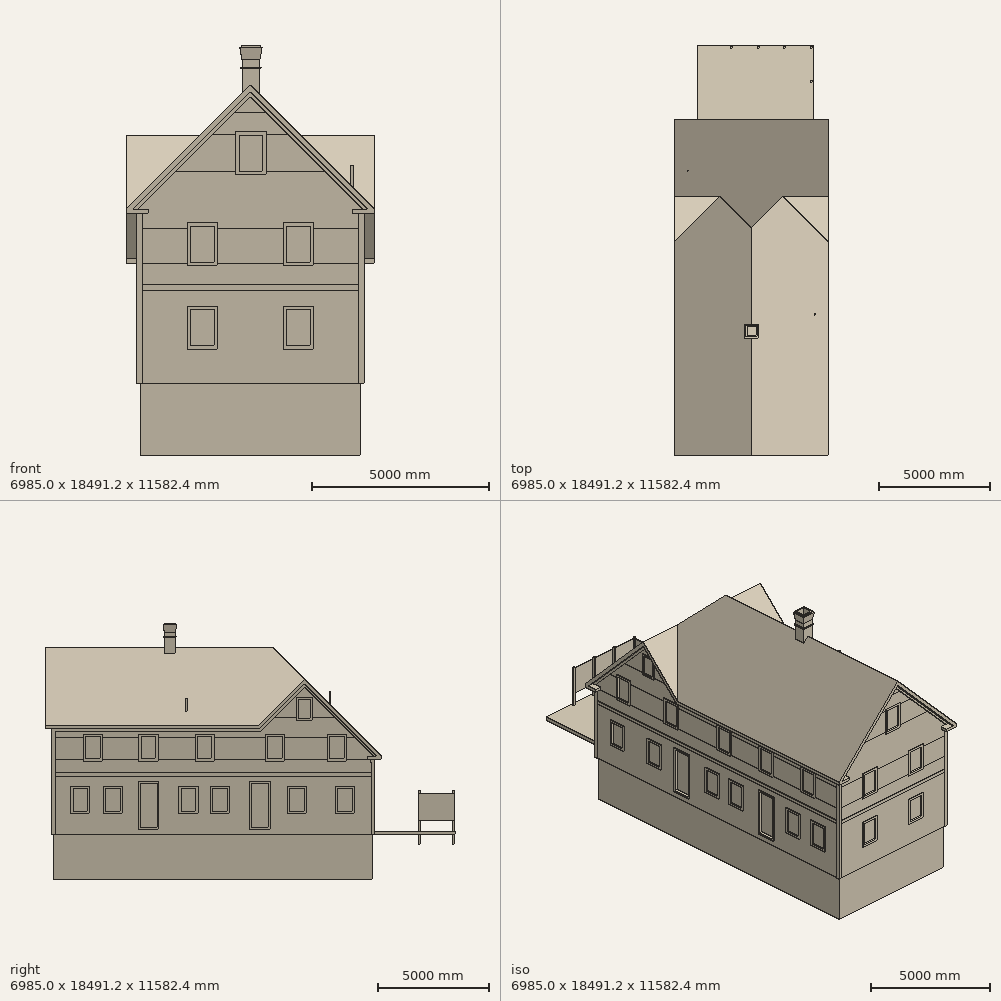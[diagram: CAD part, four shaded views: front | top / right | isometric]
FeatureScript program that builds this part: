
annotation { "Feature Type Name" : "Feature", "Feature Type Description" : "" }
export const myFeature = defineFeature(function(context is Context, id is Id, definition is map)
    precondition{}
    {
        {
            var Q0;
            Q0=qCreatedBy(makeId("Top.planeOp"),FACE);
            var sketch = newSketch(context, id + "F0", { "sketchPlane" : qUnion([Q0])});
            skLineSegment(sketch, "E0.bottom", {"start": v(0, 0) * mm, "end": v(-6985, 0) * mm});
            skLineSegment(sketch, "E0.top", {"start": v(0, 15138.4) * mm, "end": v(-6985, 15138.4) * mm});
            skLineSegment(sketch, "E0.left", {"start": v(0, 0) * mm, "end": v(0, 15138.4) * mm});
            skLineSegment(sketch, "E0.right", {"start": v(-6985, 0) * mm, "end": v(-6985, 15138.4) * mm});
            skSolve(sketch);
        }
        {
            var Q0;
            Q0 = qSketchRegion(id + "F0", true);
            extrude(context, id + "F1", {"entities" : qUnion([Q0]), "depth" : 4953 * mm});
        }
        {
            var Q0;
            Q0=makeQuery(id+"F1.opExtrude","SWEPT_FACE",FACE,{"disambiguationData":[OSD([sQuery(id+"F0.wireOp",EDGE,"E0.bottom")])]});
            var sketch = newSketch(context, id + "F2", { "sketchPlane" : qUnion([Q0])});
            skLineSegment(sketch, "E1", {"start": v(-6985, 4953) * mm, "end": v(0, 4953) * mm});
            skLineSegment(sketch, "E2", {"start": v(0, 4953) * mm, "end": v(-3492.5, 8445.5) * mm});
            skLineSegment(sketch, "E3", {"start": v(-3492.5, 8445.5) * mm, "end": v(-6985, 4953) * mm});
            skSolve(sketch);
        }
        {
            var Q0;
            Q0=makeQuery(id+"F2.imprint","IMPRINT",FACE,{"disambiguationData":[TD([[makeQuery(id+"F2.imprint","IMPRINT",EDGE,{"derivedFrom":sQuery(id+"F2.wireOp",EDGE,"E1")}),-1.0]])]});
            var Q1;
            Q1=makeQuery(id+"F1.opExtrude","SWEPT_FACE",FACE,{"disambiguationData":[OSD([sQuery(id+"F0.wireOp",EDGE,"E0.top")])]});
            extrude(context, id + "F3", {"entities" : qUnion([Q0]), "operationType" : NewBodyOperationType.ADD, "endBound" : BoundingType.UP_TO_SURFACE, "oppositeDirection" : true, "endBoundEntityFace" : qUnion([Q1]), "depth" : 25.4 * mm});
        }
        {
            var Q0;
            Q0=makeQuery(id+"F1.opExtrude","SWEPT_FACE",FACE,{"disambiguationData":[OSD([sQuery(id+"F0.wireOp",EDGE,"E0.left")])]});
            var sketch = newSketch(context, id + "F4", { "sketchPlane" : qUnion([Q0])});
            skLineSegment(sketch, "E4", {"start": v(15138.4, 3556) * mm, "end": v(10248.9, 8445.5) * mm});
            skLineSegment(sketch, "E5", {"start": v(10248.9, 8445.5) * mm, "end": v(15138.4, 8445.5) * mm});
            skLineSegment(sketch, "E6", {"start": v(15138.4, 8445.5) * mm, "end": v(15138.4, 3556) * mm});
            skSolve(sketch);
        }
        {
            var Q0;
            {var subQ0=sQuery(id+"F4.wireOp",EDGE,"E5");Q0=makeQuery(id+"F4.imprint","IMPRINT",FACE,{"disambiguationData":[TD([[makeQuery(id+"F4.imprint","IMPRINT",EDGE,{"derivedFrom":subQ0}),-1.0]])]});}
            var Q1;
            {var subQ0=sQuery(id+"F4.wireOp",EDGE,"E6");var subQ1=sQuery(id+"F4.wireOp",EDGE,"E4");var subQ2=sQuery(id+"F0.wireOp",EDGE,"E0.left");var subQ3=makeQuery(id+"F4.imprint","INTERSECT",VERTEX,{"derivedFrom":[makeQuery(id+"F1.opExtrude","SWEPT_EDGE",EDGE,{"disambiguationData":[OSD([sQuery(id+"F0.wireOp",EDGE,"E0.top"),subQ2])]}),subQ1,subQ0]});Q1=makeQuery(id+"F4.imprint","IMPRINT",FACE,{"disambiguationData":[TD([[makeQuery(id+"F4.imprint","IMPRINT",EDGE,{"disambiguationData":[TD([[subQ3,-1.0]])],"derivedFrom":subQ1}),-1.0]])]});}
            extrude(context, id + "F5", {"entities" : qUnion([Q0, Q1]), "operationType" : NewBodyOperationType.REMOVE, "endBound" : BoundingType.THROUGH_ALL, "oppositeDirection" : true, "depth" : 25.4 * mm});
        }
        {
            var Q0;
            Q0=makeQuery(id+"F1.opExtrude","SWEPT_FACE",FACE,{"disambiguationData":[OSD([sQuery(id+"F0.wireOp",EDGE,"E0.left")])]});
            var Q1;
            Q1=makeQuery(id+"F5.boolean.opBoolean","INTERSECT",VERTEX,{"derivedFrom":[makeQuery(id+"F3.opExtrude","SWEPT_FACE",FACE,{"disambiguationData":[OSD([sQuery(id+"F2.wireOp",EDGE,"E2")])]}),makeQuery(id+"F3.opExtrude","SWEPT_FACE",FACE,{"disambiguationData":[OSD([sQuery(id+"F2.wireOp",EDGE,"E3")])]}),makeQuery(id+"F5.opExtrude","SWEPT_FACE",FACE,{"disambiguationData":[OSD([sQuery(id+"F4.wireOp",EDGE,"E4")])]})]});
            cPlane(context, id + "F6", {"entities" : qUnion([Q0, Q1]), "cplaneType" : CPlaneType.PLANE_POINT, "offset" : 25.4 * mm, "width" : 152.4 * mm, "height" : 152.4 * mm});
        }
        {
            var Q0;
            Q0=qCreatedBy(id+"F6.planeOp",FACE);
            var sketch = newSketch(context, id + "F7", { "sketchPlane" : qUnion([Q0])});
            skLineSegment(sketch, "E7", {"start": v(11685.74, 7008.66) * mm, "end": v(9630.08, 4953) * mm});
            skLineSegment(sketch, "E8", {"start": v(11685.74, 7008.66) * mm, "end": v(15138.4, 3556) * mm});
            skLineSegment(sketch, "E9", {"start": v(15138.4, 3556) * mm, "end": v(9630.08, 4953) * mm});
            skSolve(sketch);
        }
        {
            var Q0;
            Q0 = qSketchRegion(id + "F7", true);
            var Q1;
            Q1=makeQuery(id+"F1.opExtrude","SWEPT_FACE",FACE,{"disambiguationData":[OSD([sQuery(id+"F0.wireOp",EDGE,"E0.left")])]});
            var Q2;
            Q2=makeQuery(id+"F1.opExtrude","SWEPT_FACE",FACE,{"disambiguationData":[OSD([sQuery(id+"F0.wireOp",EDGE,"E0.right")])]});
            extrude(context, id + "F8", {"entities" : qUnion([Q0]), "operationType" : NewBodyOperationType.ADD, "endBound" : BoundingType.UP_TO_SURFACE, "endBoundEntityFace" : qUnion([Q1]), "depth" : 25.4 * mm, "hasSecondDirection" : true, "secondDirectionBound" : SecondDirectionBoundingType.UP_TO_SURFACE, "secondDirectionOppositeDirection" : true, "secondDirectionBoundEntityFace" : qUnion([Q2]), "secondDirectionDepth" : 25.4 * mm});
        }
        {
            var Q0;
            Q0=makeQuery(id+"F8.boolean.opBoolean","MERGE",FACE,{"derivedFrom":[makeQuery(id+"F1.opExtrude","SWEPT_FACE",FACE,{"disambiguationData":[OSD([sQuery(id+"F0.wireOp",EDGE,"E0.left")])]}),makeQuery(id+"F8.opExtrude","CAP_FACE",FACE,{"disambiguationData":[OSD([sQuery(id+"F7.wireOp",EDGE,"E7"),sQuery(id+"F7.wireOp",EDGE,"E8"),sQuery(id+"F7.wireOp",EDGE,"E9")])],"isStart":false})]});
            var sketch = newSketch(context, id + "F9", { "sketchPlane" : qUnion([Q0])});
            skLineSegment(sketch, "E10", {"start": v(11685.74, 6793.13) * mm, "end": v(9630.08, 4737.47) * mm});
            skLineSegment(sketch, "E11", {"start": v(11685.74, 6793.13) * mm, "end": v(14948.27, 3530.6) * mm});
            skLineSegment(sketch, "E12", {"start": v(14948.27, 3530.6) * mm, "end": v(14528.8, 3530.6) * mm});
            skLineSegment(sketch, "E13", {"start": v(14528.8, 3530.6) * mm, "end": v(14528.8, 3403.6) * mm});
            skLineSegment(sketch, "E14", {"start": v(14528.8, 3403.6) * mm, "end": v(15303.14, 3403.6) * mm});
            skLineSegment(sketch, "E15", {"start": v(9630.08, 4737.47) * mm, "end": v(9630.08, 0) * mm});
            skLineSegment(sketch, "E16", {"start": v(9630.08, 0) * mm, "end": v(15138.4, 0) * mm});
            skLineSegment(sketch, "E17", {"start": v(15303.14, 3403.6) * mm, "end": v(15138.4, 0) * mm});
            skSolve(sketch);
        }
        {
            var Q0;
            Q0 = qSketchRegion(id + "F9", true);
            extrude(context, id + "F10", {"entities" : qUnion([Q0]), "operationType" : NewBodyOperationType.REMOVE, "oppositeDirection" : true, "depth" : 304.8 * mm});
        }
        {
            var Q0;
            Q0=makeQuery(id+"F8.boolean.opBoolean","MERGE",FACE,{"derivedFrom":[makeQuery(id+"F1.opExtrude","SWEPT_FACE",FACE,{"disambiguationData":[OSD([sQuery(id+"F0.wireOp",EDGE,"E0.right")])]}),makeQuery(id+"F8.opExtrude","CAP_FACE",FACE,{"disambiguationData":[OSD([sQuery(id+"F7.wireOp",EDGE,"E7"),sQuery(id+"F7.wireOp",EDGE,"E8"),sQuery(id+"F7.wireOp",EDGE,"E9")])],"isStart":true})]});
            var sketch = newSketch(context, id + "F11", { "sketchPlane" : qUnion([Q0])});
            skLineSegment(sketch, "E18.0.0", {"start": v(-15138.4, 0) * mm, "end": v(-15138.4, 3403.6) * mm});
            skLineSegment(sketch, "E18.0.1", {"start": v(-15138.4, 3403.6) * mm, "end": v(-14528.8, 3403.6) * mm});
            skLineSegment(sketch, "E18.0.2", {"start": v(-14528.8, 3403.6) * mm, "end": v(-14528.8, 3530.6) * mm});
            skLineSegment(sketch, "E18.0.3", {"start": v(-14528.8, 3530.6) * mm, "end": v(-14948.27, 3530.6) * mm});
            skLineSegment(sketch, "E18.0.4", {"start": v(-14948.27, 3530.6) * mm, "end": v(-11685.74, 6793.13) * mm});
            skLineSegment(sketch, "E18.0.5", {"start": v(-11685.74, 6793.13) * mm, "end": v(-9630.08, 4737.47) * mm});
            skLineSegment(sketch, "E18.0.6", {"start": v(-9630.08, 4737.47) * mm, "end": v(-9630.08, 0) * mm});
            skLineSegment(sketch, "E18.0.7", {"start": v(-9630.08, 0) * mm, "end": v(-15138.4, 0) * mm});
            skSolve(sketch);
        }
        {
            var Q0;
            Q0 = qSketchRegion(id + "F11", true);
            extrude(context, id + "F12", {"entities" : qUnion([Q0]), "operationType" : NewBodyOperationType.REMOVE, "oppositeDirection" : true, "depth" : 304.8 * mm});
        }
        {
            var Q0;
            Q0=makeQuery(id+"F10.boolean.opBoolean","COPY",FACE,{"derivedFrom":makeQuery(id+"F10.opExtrude","CAP_FACE",FACE,{"disambiguationData":[OSD([sQuery(id+"F9.wireOp",EDGE,"E10"),sQuery(id+"F9.wireOp",EDGE,"E11"),sQuery(id+"F9.wireOp",EDGE,"E12"),sQuery(id+"F9.wireOp",EDGE,"E13"),sQuery(id+"F9.wireOp",EDGE,"E14"),sQuery(id+"F9.wireOp",EDGE,"E15"),sQuery(id+"F9.wireOp",EDGE,"E16"),sQuery(id+"F9.wireOp",EDGE,"E17")])],"isStart":false})});
            var sketch = newSketch(context, id + "F13", { "sketchPlane" : qUnion([Q0])});
            skLineSegment(sketch, "E19.bottom", {"start": v(15138.4, 0) * mm, "end": v(14833.6, 0) * mm});
            skLineSegment(sketch, "E19.top", {"start": v(15138.4, 3403.6) * mm, "end": v(14833.6, 3403.6) * mm});
            skLineSegment(sketch, "E19.left", {"start": v(15138.4, 0) * mm, "end": v(15138.4, 3403.6) * mm});
            skLineSegment(sketch, "E19.right", {"start": v(14833.6, 0) * mm, "end": v(14833.6, 3403.6) * mm});
            skSolve(sketch);
        }
        {
            var Q0;
            Q0 = qSketchRegion(id + "F13", true);
            extrude(context, id + "F14", {"entities" : qUnion([Q0]), "operationType" : NewBodyOperationType.REMOVE, "endBound" : BoundingType.THROUGH_ALL, "oppositeDirection" : true, "depth" : 25.4 * mm});
        }
        {
            var Q0;
            Q0=makeQuery(id+"F3.boolean.opBoolean","MERGE",FACE,{"derivedFrom":[makeQuery(id+"F1.opExtrude","SWEPT_FACE",FACE,{"disambiguationData":[OSD([sQuery(id+"F0.wireOp",EDGE,"E0.bottom")])]}),makeQuery(id+"F3.opExtrude","CAP_FACE",FACE,{"disambiguationData":[OSD([sQuery(id+"F2.wireOp",EDGE,"E1"),sQuery(id+"F2.wireOp",EDGE,"E2"),sQuery(id+"F2.wireOp",EDGE,"E3")])],"isStart":true})]});
            var sketch = newSketch(context, id + "F15", { "sketchPlane" : qUnion([Q0])});
            skLineSegment(sketch, "E20", {"start": v(-3492.5, 8229.97) * mm, "end": v(-190.13, 4927.6) * mm});
            skLineSegment(sketch, "E21", {"start": v(-190.13, 4927.6) * mm, "end": v(-609.6, 4927.6) * mm});
            skLineSegment(sketch, "E22", {"start": v(-609.6, 4927.6) * mm, "end": v(-609.6, 4800.6) * mm});
            skLineSegment(sketch, "E23", {"start": v(-609.6, 4800.6) * mm, "end": v(323.7, 4800.6) * mm});
            skLineSegment(sketch, "E24", {"start": v(323.7, 4800.6) * mm, "end": v(323.7, 0) * mm});
            skLineSegment(sketch, "E25", {"start": v(323.7, 0) * mm, "end": v(-3492.5, 0) * mm});
            skLineSegment(sketch, "E26.MirrorCS", {"start": v(-7308.7, 0) * mm, "end": v(-3492.5, 0) * mm});
            skLineSegment(sketch, "E27.MirrorCS", {"start": v(-7308.7, 4800.6) * mm, "end": v(-7308.7, 0) * mm});
            skLineSegment(sketch, "E28.MirrorCS", {"start": v(-6375.4, 4800.6) * mm, "end": v(-7308.7, 4800.6) * mm});
            skLineSegment(sketch, "E29.MirrorCS", {"start": v(-6375.4, 4927.6) * mm, "end": v(-6375.4, 4800.6) * mm});
            skLineSegment(sketch, "E30.MirrorCS", {"start": v(-3492.5, 8229.97) * mm, "end": v(-6794.87, 4927.6) * mm});
            skLineSegment(sketch, "E31.MirrorCS", {"start": v(-6794.87, 4927.6) * mm, "end": v(-6375.4, 4927.6) * mm});
            skSolve(sketch);
        }
        {
            var Q0;
            Q0 = qSketchRegion(id + "F15", true);
            extrude(context, id + "F16", {"entities" : qUnion([Q0]), "operationType" : NewBodyOperationType.REMOVE, "oppositeDirection" : true, "depth" : 304.8 * mm});
        }
        {
            var Q0;
            Q0=makeQuery(id+"F16.boolean.opBoolean","COPY",FACE,{"derivedFrom":makeQuery(id+"F16.opExtrude","CAP_FACE",FACE,{"disambiguationData":[OSD([sQuery(id+"F15.wireOp",EDGE,"E20"),sQuery(id+"F15.wireOp",EDGE,"E21"),sQuery(id+"F15.wireOp",EDGE,"E22"),sQuery(id+"F15.wireOp",EDGE,"E23"),sQuery(id+"F15.wireOp",EDGE,"E24"),sQuery(id+"F15.wireOp",EDGE,"E25"),sQuery(id+"F15.wireOp",EDGE,"E26.MirrorCS"),sQuery(id+"F15.wireOp",EDGE,"E27.MirrorCS"),sQuery(id+"F15.wireOp",EDGE,"E28.MirrorCS"),sQuery(id+"F15.wireOp",EDGE,"E29.MirrorCS"),sQuery(id+"F15.wireOp",EDGE,"E30.MirrorCS"),sQuery(id+"F15.wireOp",EDGE,"E31.MirrorCS")])],"isStart":false})});
            var sketch = newSketch(context, id + "F17", { "sketchPlane" : qUnion([Q0])});
            skLineSegment(sketch, "E32.bottom", {"start": v(0, 0) * mm, "end": v(-304.8, 0) * mm});
            skLineSegment(sketch, "E32.top", {"start": v(0, 4800.6) * mm, "end": v(-304.8, 4800.6) * mm});
            skLineSegment(sketch, "E32.left", {"start": v(0, 0) * mm, "end": v(0, 4800.6) * mm});
            skLineSegment(sketch, "E32.right", {"start": v(-304.8, 0) * mm, "end": v(-304.8, 4800.6) * mm});
            skLineSegment(sketch, "E33.MirrorCS", {"start": v(-6985, 4800.6) * mm, "end": v(-6680.2, 4800.6) * mm});
            skLineSegment(sketch, "E34.MirrorCS", {"start": v(-6985, 0) * mm, "end": v(-6680.2, 0) * mm});
            skLineSegment(sketch, "E35.MirrorCS", {"start": v(-6680.2, 0) * mm, "end": v(-6680.2, 4800.6) * mm});
            skLineSegment(sketch, "E36.MirrorCS", {"start": v(-6985, 0) * mm, "end": v(-6985, 4800.6) * mm});
            skSolve(sketch);
        }
        {
            var Q0;
            Q0 = qSketchRegion(id + "F17", true);
            var Q1;
            Q1=makeQuery(id+"F10.boolean.opBoolean","COPY",FACE,{"derivedFrom":makeQuery(id+"F10.opExtrude","SWEPT_FACE",FACE,{"disambiguationData":[OSD([sQuery(id+"F9.wireOp",EDGE,"E15")])]})});
            extrude(context, id + "F18", {"entities" : qUnion([Q0]), "operationType" : NewBodyOperationType.REMOVE, "oppositeDirection" : true, "endBoundEntityFace" : qUnion([Q1]), "depth" : 10617.2 * mm});
        }
        {
            var Q0;
            Q0=makeQuery(id+"F14.boolean.opBoolean","MERGE",FACE,{"derivedFrom":[makeQuery(id+"F10.boolean.opBoolean","COPY",FACE,{"derivedFrom":makeQuery(id+"F10.opExtrude","SWEPT_FACE",FACE,{"disambiguationData":[OSD([sQuery(id+"F9.wireOp",EDGE,"E14")])]})}),makeQuery(id+"F12.boolean.opBoolean","COPY",FACE,{"derivedFrom":makeQuery(id+"F12.opExtrude","SWEPT_FACE",FACE,{"disambiguationData":[OSD([sQuery(id+"F11.wireOp",EDGE,"E18.0.1")])]})}),makeQuery(id+"F14.opExtrude","SWEPT_FACE",FACE,{"disambiguationData":[OSD([sQuery(id+"F13.wireOp",EDGE,"E19.top")])]})]});
            cPlane(context, id + "F19", {"entities" : qUnion([Q0]), "cplaneType" : CPlaneType.OFFSET, "offset" : 609.6 * mm, "width" : 152.4 * mm, "height" : 152.4 * mm});
        }
        {
            var Q0;
            Q0=qCreatedBy(id+"F19.planeOp",FACE);
            var sketch = newSketch(context, id + "F20", { "sketchPlane" : qUnion([Q0])});
            skLineSegment(sketch, "E37.0", {"start": v(-285.75, -285.75) * mm, "end": v(-6699.25, -285.75) * mm});
            skLineSegment(sketch, "E37.1", {"start": v(-285.75, -14852.65) * mm, "end": v(-285.75, -285.75) * mm});
            skLineSegment(sketch, "E37.2", {"start": v(-6699.25, -14852.65) * mm, "end": v(-285.75, -14852.65) * mm});
            skLineSegment(sketch, "E37.3", {"start": v(-6699.25, -285.75) * mm, "end": v(-6699.25, -14852.65) * mm});
            skSolve(sketch);
        }
        {
            var Q0;
            Q0 = qSketchRegion(id + "F20", true);
            extrude(context, id + "F21", {"entities" : qUnion([Q0]), "operationType" : NewBodyOperationType.ADD, "depth" : 152.4 * mm});
        }
        {
            var Q0;
            {var subQ1=sQuery(id+"F9.wireOp",EDGE,"E14");var subQ2=sQuery(id+"F9.wireOp",EDGE,"E10");var subQ3=sQuery(id+"F9.wireOp",EDGE,"E11");var subQ4=sQuery(id+"F9.wireOp",EDGE,"E13");var subQ5=sQuery(id+"F9.wireOp",EDGE,"E12");Q0=makeQuery(id+"F21.boolean.opBoolean","SPLIT",FACE,{"disambiguationData":[TD([makeQuery(id+"F10.boolean.opBoolean","COPY",FACE,{"derivedFrom":makeQuery(id+"F10.opExtrude","SWEPT_FACE",FACE,{"disambiguationData":[OSD([subQ2])]})})])],"derivedFrom":makeQuery(id+"F18.boolean.opBoolean","MERGE",FACE,{"derivedFrom":[makeQuery(id+"F10.boolean.opBoolean","COPY",FACE,{"derivedFrom":makeQuery(id+"F10.opExtrude","CAP_FACE",FACE,{"disambiguationData":[OSD([subQ2,subQ3,subQ5,subQ4,subQ1,sQuery(id+"F9.wireOp",EDGE,"E15"),sQuery(id+"F9.wireOp",EDGE,"E16"),sQuery(id+"F9.wireOp",EDGE,"E17")])],"isStart":false})}),makeQuery(id+"F18.opExtrude","SWEPT_FACE",FACE,{"disambiguationData":[OSD([sQuery(id+"F17.wireOp",EDGE,"E32.right")])]})]})});}
            var sketch = newSketch(context, id + "F22", { "sketchPlane" : qUnion([Q0])});
            skLineSegment(sketch, "E38", {"start": v(304.8, 4800.6) * mm, "end": v(304.8, 4648.2) * mm});
            skLineSegment(sketch, "E39", {"start": v(304.8, 4648.2) * mm, "end": v(9684.5, 4648.2) * mm});
            skLineSegment(sketch, "E40", {"start": v(9684.5, 4648.2) * mm, "end": v(11685.74, 6649.45) * mm});
            skLineSegment(sketch, "E41", {"start": v(11685.74, 6649.45) * mm, "end": v(14804.59, 3530.6) * mm});
            skSolve(sketch);
        }
        {
            var Q0;
            Q0=makeQuery(id+"F22.imprint","IMPRINT",FACE,{"disambiguationData":[TD([[makeQuery(id+"F22.imprint","IMPRINT",EDGE,{"derivedFrom":sQuery(id+"F22.wireOp",EDGE,"E38")}),-1.0]])]});
            extrude(context, id + "F23", {"entities" : qUnion([Q0]), "operationType" : NewBodyOperationType.ADD, "depth" : 25.4 * mm});
        }
        {
            var Q0;
            {var subQ1=sQuery(id+"F11.wireOp",EDGE,"E18.0.5");var subQ2=sQuery(id+"F11.wireOp",EDGE,"E18.0.2");var subQ3=sQuery(id+"F11.wireOp",EDGE,"E18.0.1");var subQ4=sQuery(id+"F11.wireOp",EDGE,"E18.0.4");var subQ5=sQuery(id+"F11.wireOp",EDGE,"E18.0.3");Q0=makeQuery(id+"F21.boolean.opBoolean","SPLIT",FACE,{"disambiguationData":[TD([makeQuery(id+"F10.boolean.opBoolean","COPY",FACE,{"derivedFrom":makeQuery(id+"F10.opExtrude","SWEPT_FACE",FACE,{"disambiguationData":[OSD([sQuery(id+"F9.wireOp",EDGE,"E14")])]})})])],"derivedFrom":makeQuery(id+"F18.boolean.opBoolean","MERGE",FACE,{"derivedFrom":[makeQuery(id+"F12.boolean.opBoolean","COPY",FACE,{"derivedFrom":makeQuery(id+"F12.opExtrude","CAP_FACE",FACE,{"disambiguationData":[OSD([sQuery(id+"F11.wireOp",EDGE,"E18.0.0"),subQ3,subQ2,subQ5,subQ4,subQ1,sQuery(id+"F11.wireOp",EDGE,"E18.0.6"),sQuery(id+"F11.wireOp",EDGE,"E18.0.7")])],"isStart":false})}),makeQuery(id+"F18.opExtrude","SWEPT_FACE",FACE,{"disambiguationData":[OSD([sQuery(id+"F17.wireOp",EDGE,"E35.MirrorCS")])]})]})});}
            var sketch = newSketch(context, id + "F24", { "sketchPlane" : qUnion([Q0])});
            skLineSegment(sketch, "E42.0.0", {"start": v(-304.8, 4800.6) * mm, "end": v(-304.8, 4648.2) * mm});
            skLineSegment(sketch, "E42.0.1", {"start": v(-304.8, 4648.2) * mm, "end": v(-9684.5, 4648.2) * mm});
            skLineSegment(sketch, "E42.0.2", {"start": v(-9684.5, 4648.2) * mm, "end": v(-11685.74, 6649.45) * mm});
            skLineSegment(sketch, "E42.0.3", {"start": v(-11685.74, 6649.45) * mm, "end": v(-14804.59, 3530.6) * mm});
            skLineSegment(sketch, "E42.0.4", {"start": v(-14804.59, 3530.6) * mm, "end": v(-14948.27, 3530.6) * mm});
            skLineSegment(sketch, "E42.0.5", {"start": v(-14948.27, 3530.6) * mm, "end": v(-11685.74, 6793.13) * mm});
            skLineSegment(sketch, "E42.0.6", {"start": v(-11685.74, 6793.13) * mm, "end": v(-9693.2, 4800.6) * mm});
            skLineSegment(sketch, "E42.0.7", {"start": v(-9693.2, 4800.6) * mm, "end": v(-304.8, 4800.6) * mm});
            skSolve(sketch);
        }
        {
            var Q0;
            Q0 = qSketchRegion(id + "F24", true);
            extrude(context, id + "F25", {"entities" : qUnion([Q0]), "operationType" : NewBodyOperationType.ADD, "depth" : 25.4 * mm});
        }
        {
            var Q0;
            {var subQ0=sQuery(id+"F15.wireOp",EDGE,"E31.MirrorCS");var subQ1=sQuery(id+"F15.wireOp",EDGE,"E30.MirrorCS");var subQ2=sQuery(id+"F15.wireOp",EDGE,"E29.MirrorCS");var subQ3=sQuery(id+"F15.wireOp",EDGE,"E28.MirrorCS");var subQ4=sQuery(id+"F15.wireOp",EDGE,"E23");var subQ5=sQuery(id+"F15.wireOp",EDGE,"E22");var subQ6=sQuery(id+"F15.wireOp",EDGE,"E21");var subQ7=sQuery(id+"F15.wireOp",EDGE,"E20");Q0=makeQuery(id+"F25.boolean.opBoolean","MERGE",FACE,{"derivedFrom":[makeQuery(id+"F23.boolean.opBoolean","MERGE",FACE,{"derivedFrom":[makeQuery(id+"F21.boolean.opBoolean","SPLIT",FACE,{"disambiguationData":[TD([makeQuery(id+"F16.boolean.opBoolean","COPY",FACE,{"derivedFrom":makeQuery(id+"F16.opExtrude","SWEPT_FACE",FACE,{"disambiguationData":[OSD([subQ7])]})})])],"derivedFrom":makeQuery(id+"F16.boolean.opBoolean","COPY",FACE,{"derivedFrom":makeQuery(id+"F16.opExtrude","CAP_FACE",FACE,{"disambiguationData":[OSD([subQ7,subQ6,subQ5,subQ4,sQuery(id+"F15.wireOp",EDGE,"E24"),sQuery(id+"F15.wireOp",EDGE,"E25"),sQuery(id+"F15.wireOp",EDGE,"E26.MirrorCS"),sQuery(id+"F15.wireOp",EDGE,"E27.MirrorCS"),subQ3,subQ2,subQ1,subQ0])],"isStart":false})})}),makeQuery(id+"F23.opExtrude","SWEPT_FACE",FACE,{"disambiguationData":[OSD([sQuery(id+"F22.wireOp",EDGE,"E38")])]})]}),makeQuery(id+"F25.opExtrude","SWEPT_FACE",FACE,{"disambiguationData":[OSD([sQuery(id+"F24.wireOp",EDGE,"E42.0.0")])]})]});}
            var sketch = newSketch(context, id + "F26", { "sketchPlane" : qUnion([Q0])});
            skLineSegment(sketch, "E43", {"start": v(-6651.19, 4927.6) * mm, "end": v(-3492.5, 8086.29) * mm});
            skLineSegment(sketch, "E44", {"start": v(-3492.5, 8086.29) * mm, "end": v(-333.81, 4927.6) * mm});
            skSolve(sketch);
        }
        {
            var Q0;
            {var subQ5=sQuery(id+"F26.wireOp",EDGE,"E43");Q0=makeQuery(id+"F26.imprint","IMPRINT",FACE,{"disambiguationData":[TD([[makeQuery(id+"F26.imprint","IMPRINT",EDGE,{"derivedFrom":subQ5}),1.0]])]});}
            extrude(context, id + "F27", {"entities" : qUnion([Q0]), "operationType" : NewBodyOperationType.ADD, "depth" : 25.4 * mm});
        }
        {
            var Q0;
            {var subQ1=sQuery(id+"F9.wireOp",EDGE,"E14");var subQ2=sQuery(id+"F9.wireOp",EDGE,"E10");var subQ3=sQuery(id+"F9.wireOp",EDGE,"E11");var subQ4=sQuery(id+"F9.wireOp",EDGE,"E13");var subQ5=sQuery(id+"F9.wireOp",EDGE,"E12");Q0=makeQuery(id+"F21.boolean.opBoolean","SPLIT",FACE,{"disambiguationData":[TD([makeQuery(id+"F10.boolean.opBoolean","COPY",FACE,{"derivedFrom":makeQuery(id+"F10.opExtrude","SWEPT_FACE",FACE,{"disambiguationData":[OSD([subQ2])]})})])],"derivedFrom":makeQuery(id+"F18.boolean.opBoolean","MERGE",FACE,{"derivedFrom":[makeQuery(id+"F10.boolean.opBoolean","COPY",FACE,{"derivedFrom":makeQuery(id+"F10.opExtrude","CAP_FACE",FACE,{"disambiguationData":[OSD([subQ2,subQ3,subQ5,subQ4,subQ1,sQuery(id+"F9.wireOp",EDGE,"E15"),sQuery(id+"F9.wireOp",EDGE,"E16"),sQuery(id+"F9.wireOp",EDGE,"E17")])],"isStart":false})}),makeQuery(id+"F18.opExtrude","SWEPT_FACE",FACE,{"disambiguationData":[OSD([sQuery(id+"F17.wireOp",EDGE,"E32.right")])]})]})});}
            var sketch = newSketch(context, id + "F28", { "sketchPlane" : qUnion([Q0])});
            skLineSegment(sketch, "E45.bottom", {"start": v(14655.8, 3251.2) * mm, "end": v(14859, 3251.2) * mm});
            skLineSegment(sketch, "E45.top", {"start": v(14655.8, 3403.6) * mm, "end": v(14859, 3403.6) * mm});
            skLineSegment(sketch, "E45.left", {"start": v(14655.8, 3251.2) * mm, "end": v(14655.8, 3403.6) * mm});
            skLineSegment(sketch, "E45.right", {"start": v(14859, 3251.2) * mm, "end": v(14859, 3403.6) * mm});
            skSolve(sketch);
        }
        {
            var Q0;
            Q0 = qSketchRegion(id + "F28", true);
            extrude(context, id + "F29", {"entities" : qUnion([Q0]), "operationType" : NewBodyOperationType.ADD, "depth" : 25.4 * mm, "hasSecondDirection" : true, "secondDirectionOppositeDirection" : true, "secondDirectionDepth" : 6400.8 * mm});
        }
        {
            var Q0;
            Q0=makeQuery(id+"F1.opExtrude","CAP_FACE",FACE,{"disambiguationData":[OSD([sQuery(id+"F0.wireOp",EDGE,"E0.bottom"),sQuery(id+"F0.wireOp",EDGE,"E0.top"),sQuery(id+"F0.wireOp",EDGE,"E0.left"),sQuery(id+"F0.wireOp",EDGE,"E0.right")])],"isStart":true});
            var sketch = newSketch(context, id + "F30", { "sketchPlane" : qUnion([Q0])});
            skLineSegment(sketch, "E46.bottom", {"start": v(-431.8, -279.4) * mm, "end": v(-279.4, -279.4) * mm});
            skLineSegment(sketch, "E46.top", {"start": v(-431.8, -431.8) * mm, "end": v(-279.4, -431.8) * mm});
            skLineSegment(sketch, "E46.left", {"start": v(-431.8, -279.4) * mm, "end": v(-431.8, -431.8) * mm});
            skLineSegment(sketch, "E46.right", {"start": v(-279.4, -279.4) * mm, "end": v(-279.4, -431.8) * mm});
            skLineSegment(sketch, "E47", {"start": v(-3492.5, -304.8) * mm, "end": v(-3492.5, -1029.25) * mm});
            skPoint(sketch, "E47.endSnap0", {"position": v(-3492.5, -304.8) * mm});
            skLineSegment(sketch, "E48.MirrorCS", {"start": v(-6553.2, -279.4) * mm, "end": v(-6705.6, -279.4) * mm});
            skLineSegment(sketch, "E49.MirrorCS", {"start": v(-6553.2, -431.8) * mm, "end": v(-6705.6, -431.8) * mm});
            skLineSegment(sketch, "E50.MirrorCS", {"start": v(-6553.2, -279.4) * mm, "end": v(-6553.2, -431.8) * mm});
            skLineSegment(sketch, "E51.MirrorCS", {"start": v(-6705.6, -279.4) * mm, "end": v(-6705.6, -431.8) * mm});
            skSolve(sketch);
        }
        {
            var Q0;
            Q0 = qSketchRegion(id + "F30", true);
            var Q1;
            Q1=makeQuery(id+"F18.boolean.opBoolean","MERGE",FACE,{"derivedFrom":[makeQuery(id+"F16.boolean.opBoolean","COPY",FACE,{"derivedFrom":makeQuery(id+"F16.opExtrude","SWEPT_FACE",FACE,{"disambiguationData":[OSD([sQuery(id+"F15.wireOp",EDGE,"E28.MirrorCS")])]})}),makeQuery(id+"F18.opExtrude","SWEPT_FACE",FACE,{"disambiguationData":[OSD([sQuery(id+"F17.wireOp",EDGE,"E33.MirrorCS")])]})]});
            extrude(context, id + "F31", {"entities" : qUnion([Q0]), "operationType" : NewBodyOperationType.ADD, "endBound" : BoundingType.UP_TO_SURFACE, "oppositeDirection" : true, "endBoundEntityFace" : qUnion([Q1]), "depth" : 25.4 * mm});
        }
        {
            var Q0;
            Q0=makeQuery(id+"F31.boolean.opBoolean","MERGE",FACE,{"derivedFrom":[makeQuery(id+"F1.opExtrude","CAP_FACE",FACE,{"disambiguationData":[OSD([sQuery(id+"F0.wireOp",EDGE,"E0.bottom"),sQuery(id+"F0.wireOp",EDGE,"E0.top"),sQuery(id+"F0.wireOp",EDGE,"E0.left"),sQuery(id+"F0.wireOp",EDGE,"E0.right")])],"isStart":true}),makeQuery(id+"F31.opExtrude","CAP_FACE",FACE,{"disambiguationData":[OSD([sQuery(id+"F30.wireOp",EDGE,"E46.bottom"),sQuery(id+"F30.wireOp",EDGE,"E46.top"),sQuery(id+"F30.wireOp",EDGE,"E46.left"),sQuery(id+"F30.wireOp",EDGE,"E46.right")])],"isStart":true}),makeQuery(id+"F31.opExtrude","CAP_FACE",FACE,{"disambiguationData":[OSD([sQuery(id+"F30.wireOp",EDGE,"E48.MirrorCS"),sQuery(id+"F30.wireOp",EDGE,"E49.MirrorCS"),sQuery(id+"F30.wireOp",EDGE,"E50.MirrorCS"),sQuery(id+"F30.wireOp",EDGE,"E51.MirrorCS")])],"isStart":true})]});
            var sketch = newSketch(context, id + "F32", { "sketchPlane" : qUnion([Q0])});
            skLineSegment(sketch, "E52.bottom", {"start": v(-6553.2, -14706.6) * mm, "end": v(-6705.6, -14706.6) * mm});
            skLineSegment(sketch, "E52.top", {"start": v(-6553.2, -14859) * mm, "end": v(-6705.6, -14859) * mm});
            skLineSegment(sketch, "E52.left", {"start": v(-6553.2, -14706.6) * mm, "end": v(-6553.2, -14859) * mm});
            skLineSegment(sketch, "E52.right", {"start": v(-6705.6, -14706.6) * mm, "end": v(-6705.6, -14859) * mm});
            skLineSegment(sketch, "E53", {"start": v(-3492.5, -14833.6) * mm, "end": v(-3492.5, -14090.53) * mm});
            skLineSegment(sketch, "E54.MirrorCS", {"start": v(-431.8, -14706.6) * mm, "end": v(-431.8, -14859) * mm});
            skLineSegment(sketch, "E55.MirrorCS", {"start": v(-279.4, -14706.6) * mm, "end": v(-279.4, -14859) * mm});
            skLineSegment(sketch, "E56.MirrorCS", {"start": v(-431.8, -14706.6) * mm, "end": v(-279.4, -14706.6) * mm});
            skLineSegment(sketch, "E57.MirrorCS", {"start": v(-431.8, -14859) * mm, "end": v(-279.4, -14859) * mm});
            skSolve(sketch);
        }
        {
            var Q0;
            Q0 = qSketchRegion(id + "F32", true);
            var Q1;
            Q1=makeQuery(id+"F14.boolean.opBoolean","MERGE",FACE,{"derivedFrom":[makeQuery(id+"F10.boolean.opBoolean","COPY",FACE,{"derivedFrom":makeQuery(id+"F10.opExtrude","SWEPT_FACE",FACE,{"disambiguationData":[OSD([sQuery(id+"F9.wireOp",EDGE,"E14")])]})}),makeQuery(id+"F12.boolean.opBoolean","COPY",FACE,{"derivedFrom":makeQuery(id+"F12.opExtrude","SWEPT_FACE",FACE,{"disambiguationData":[OSD([sQuery(id+"F11.wireOp",EDGE,"E18.0.1")])]})}),makeQuery(id+"F14.opExtrude","SWEPT_FACE",FACE,{"disambiguationData":[OSD([sQuery(id+"F13.wireOp",EDGE,"E19.top")])]})]});
            extrude(context, id + "F33", {"entities" : qUnion([Q0]), "operationType" : NewBodyOperationType.ADD, "endBound" : BoundingType.UP_TO_SURFACE, "oppositeDirection" : true, "endBoundEntityFace" : qUnion([Q1]), "depth" : 25.4 * mm});
        }
        {
            var Q0;
            {var subQ1=sQuery(id+"F9.wireOp",EDGE,"E14");var subQ2=sQuery(id+"F9.wireOp",EDGE,"E10");var subQ3=sQuery(id+"F9.wireOp",EDGE,"E11");var subQ4=sQuery(id+"F9.wireOp",EDGE,"E13");var subQ5=sQuery(id+"F9.wireOp",EDGE,"E12");Q0=makeQuery(id+"F21.boolean.opBoolean","SPLIT",FACE,{"disambiguationData":[TD([makeQuery(id+"F10.boolean.opBoolean","COPY",FACE,{"derivedFrom":makeQuery(id+"F10.opExtrude","SWEPT_FACE",FACE,{"disambiguationData":[OSD([subQ2])]})})])],"derivedFrom":makeQuery(id+"F18.boolean.opBoolean","MERGE",FACE,{"derivedFrom":[makeQuery(id+"F10.boolean.opBoolean","COPY",FACE,{"derivedFrom":makeQuery(id+"F10.opExtrude","CAP_FACE",FACE,{"disambiguationData":[OSD([subQ2,subQ3,subQ5,subQ4,subQ1,sQuery(id+"F9.wireOp",EDGE,"E15"),sQuery(id+"F9.wireOp",EDGE,"E16"),sQuery(id+"F9.wireOp",EDGE,"E17")])],"isStart":false})}),makeQuery(id+"F18.opExtrude","SWEPT_FACE",FACE,{"disambiguationData":[OSD([sQuery(id+"F17.wireOp",EDGE,"E32.right")])]})]})});}
            var sketch = newSketch(context, id + "F34", { "sketchPlane" : qUnion([Q0])});
            skLineSegment(sketch, "E58", {"start": v(14528.8, 3403.6) * mm, "end": v(431.8, 3403.6) * mm});
            skLineSegment(sketch, "E59", {"start": v(431.8, 4394.2) * mm, "end": v(13940.99, 4394.2) * mm});
            skLineSegment(sketch, "E60", {"start": v(10314.14, 5277.85) * mm, "end": v(13057.34, 5277.85) * mm});
            skSolve(sketch);
        }
        {
            var Q0;
            {var subQ0=sQuery(id+"F34.wireOp",EDGE,"E60");Q0=makeQuery(id+"F34.imprint","IMPRINT",FACE,{"disambiguationData":[TD([[makeQuery(id+"F34.imprint","IMPRINT",EDGE,{"derivedFrom":subQ0}),1.0]])]});}
            var Q1;
            {var subQ4=sQuery(id+"F34.wireOp",EDGE,"E58");Q1=makeQuery(id+"F34.imprint","IMPRINT",FACE,{"disambiguationData":[TD([[makeQuery(id+"F34.imprint","IMPRINT",EDGE,{"derivedFrom":subQ4}),-1.0]])]});}
            extrude(context, id + "F35", {"entities" : qUnion([Q0, Q1]), "operationType" : NewBodyOperationType.ADD, "depth" : 6.35 * mm});
        }
        {
            var Q0;
            {var subQ1=sQuery(id+"F11.wireOp",EDGE,"E18.0.5");var subQ2=sQuery(id+"F11.wireOp",EDGE,"E18.0.2");var subQ3=sQuery(id+"F11.wireOp",EDGE,"E18.0.1");var subQ4=sQuery(id+"F11.wireOp",EDGE,"E18.0.4");var subQ5=sQuery(id+"F11.wireOp",EDGE,"E18.0.3");Q0=makeQuery(id+"F21.boolean.opBoolean","SPLIT",FACE,{"disambiguationData":[TD([makeQuery(id+"F10.boolean.opBoolean","COPY",FACE,{"derivedFrom":makeQuery(id+"F10.opExtrude","SWEPT_FACE",FACE,{"disambiguationData":[OSD([sQuery(id+"F9.wireOp",EDGE,"E14")])]})})])],"derivedFrom":makeQuery(id+"F18.boolean.opBoolean","MERGE",FACE,{"derivedFrom":[makeQuery(id+"F12.boolean.opBoolean","COPY",FACE,{"derivedFrom":makeQuery(id+"F12.opExtrude","CAP_FACE",FACE,{"disambiguationData":[OSD([sQuery(id+"F11.wireOp",EDGE,"E18.0.0"),subQ3,subQ2,subQ5,subQ4,subQ1,sQuery(id+"F11.wireOp",EDGE,"E18.0.6"),sQuery(id+"F11.wireOp",EDGE,"E18.0.7")])],"isStart":false})}),makeQuery(id+"F18.opExtrude","SWEPT_FACE",FACE,{"disambiguationData":[OSD([sQuery(id+"F17.wireOp",EDGE,"E35.MirrorCS")])]})]})});}
            var sketch = newSketch(context, id + "F36", { "sketchPlane" : qUnion([Q0])});
            skLineSegment(sketch, "E61.0.0", {"start": v(-431.8, 3403.6) * mm, "end": v(-14528.8, 3403.6) * mm});
            skLineSegment(sketch, "E61.0.1", {"start": v(-14528.8, 3403.6) * mm, "end": v(-14528.8, 3530.6) * mm});
            skLineSegment(sketch, "E61.0.2", {"start": v(-14528.8, 3530.6) * mm, "end": v(-14804.59, 3530.6) * mm});
            skLineSegment(sketch, "E61.0.3", {"start": v(-14804.59, 3530.6) * mm, "end": v(-13940.99, 4394.2) * mm});
            skLineSegment(sketch, "E61.0.4", {"start": v(-13940.99, 4394.2) * mm, "end": v(-431.8, 4394.2) * mm});
            skLineSegment(sketch, "E61.0.5", {"start": v(-431.8, 4394.2) * mm, "end": v(-431.8, 3403.6) * mm});
            skLineSegment(sketch, "E61.1.0", {"start": v(-11685.74, 6649.45) * mm, "end": v(-10314.14, 5277.85) * mm});
            skLineSegment(sketch, "E61.1.1", {"start": v(-10314.14, 5277.85) * mm, "end": v(-13057.34, 5277.85) * mm});
            skLineSegment(sketch, "E61.1.2", {"start": v(-13057.34, 5277.85) * mm, "end": v(-11685.74, 6649.45) * mm});
            skSolve(sketch);
        }
        {
            var Q0;
            Q0=makeQuery(id+"F36.imprint","IMPRINT",FACE,{"disambiguationData":[TD([[makeQuery(id+"F36.imprint","IMPRINT",EDGE,{"derivedFrom":sQuery(id+"F36.wireOp",EDGE,"E61.0.0")}),-1.0]])]});
            var Q1;
            Q1=makeQuery(id+"F36.imprint","IMPRINT",FACE,{"disambiguationData":[TD([[makeQuery(id+"F36.imprint","IMPRINT",EDGE,{"derivedFrom":sQuery(id+"F36.wireOp",EDGE,"E61.1.0")}),1.0]])]});
            extrude(context, id + "F37", {"entities" : qUnion([Q0, Q1]), "operationType" : NewBodyOperationType.ADD, "depth" : 6.35 * mm});
        }
        {
            var Q0;
            {var subQ0=sQuery(id+"F15.wireOp",EDGE,"E31.MirrorCS");var subQ1=sQuery(id+"F15.wireOp",EDGE,"E30.MirrorCS");var subQ2=sQuery(id+"F15.wireOp",EDGE,"E29.MirrorCS");var subQ3=sQuery(id+"F15.wireOp",EDGE,"E28.MirrorCS");var subQ4=sQuery(id+"F15.wireOp",EDGE,"E23");var subQ5=sQuery(id+"F15.wireOp",EDGE,"E22");var subQ6=sQuery(id+"F15.wireOp",EDGE,"E21");var subQ7=sQuery(id+"F15.wireOp",EDGE,"E20");Q0=makeQuery(id+"F25.boolean.opBoolean","MERGE",FACE,{"derivedFrom":[makeQuery(id+"F23.boolean.opBoolean","MERGE",FACE,{"derivedFrom":[makeQuery(id+"F21.boolean.opBoolean","SPLIT",FACE,{"disambiguationData":[TD([makeQuery(id+"F16.boolean.opBoolean","COPY",FACE,{"derivedFrom":makeQuery(id+"F16.opExtrude","SWEPT_FACE",FACE,{"disambiguationData":[OSD([subQ7])]})})])],"derivedFrom":makeQuery(id+"F16.boolean.opBoolean","COPY",FACE,{"derivedFrom":makeQuery(id+"F16.opExtrude","CAP_FACE",FACE,{"disambiguationData":[OSD([subQ7,subQ6,subQ5,subQ4,sQuery(id+"F15.wireOp",EDGE,"E24"),sQuery(id+"F15.wireOp",EDGE,"E25"),sQuery(id+"F15.wireOp",EDGE,"E26.MirrorCS"),sQuery(id+"F15.wireOp",EDGE,"E27.MirrorCS"),subQ3,subQ2,subQ1,subQ0])],"isStart":false})})}),makeQuery(id+"F23.opExtrude","SWEPT_FACE",FACE,{"disambiguationData":[OSD([sQuery(id+"F22.wireOp",EDGE,"E38")])]})]}),makeQuery(id+"F25.opExtrude","SWEPT_FACE",FACE,{"disambiguationData":[OSD([sQuery(id+"F24.wireOp",EDGE,"E42.0.0")])]})]});}
            var sketch = newSketch(context, id + "F38", { "sketchPlane" : qUnion([Q0])});
            skLineSegment(sketch, "E62", {"start": v(-6553.2, 3403.6) * mm, "end": v(-431.8, 3403.6) * mm});
            skLineSegment(sketch, "E63", {"start": v(-6553.2, 4394.2) * mm, "end": v(-431.8, 4394.2) * mm});
            skLineSegment(sketch, "E64", {"start": v(-5575.3, 6003.49) * mm, "end": v(-1409.7, 6003.49) * mm});
            skSolve(sketch);
        }
        {
            var Q0;
            {var subQ0=sQuery(id+"F38.wireOp",EDGE,"E64");Q0=makeQuery(id+"F38.imprint","IMPRINT",FACE,{"disambiguationData":[TD([[makeQuery(id+"F38.imprint","IMPRINT",EDGE,{"derivedFrom":subQ0}),1.0]])]});}
            var Q1;
            {var subQ0=sQuery(id+"F38.wireOp",EDGE,"E62");Q1=makeQuery(id+"F38.imprint","IMPRINT",FACE,{"disambiguationData":[TD([[makeQuery(id+"F38.imprint","IMPRINT",EDGE,{"derivedFrom":subQ0}),1.0]])]});}
            extrude(context, id + "F39", {"entities" : qUnion([Q0, Q1]), "operationType" : NewBodyOperationType.ADD, "depth" : 6.35 * mm});
        }
        {
            var Q0;
            Q0=makeQuery(id+"F33.boolean.opBoolean","MERGE",FACE,{"derivedFrom":[makeQuery(id+"F31.boolean.opBoolean","MERGE",FACE,{"derivedFrom":[makeQuery(id+"F1.opExtrude","CAP_FACE",FACE,{"disambiguationData":[OSD([sQuery(id+"F0.wireOp",EDGE,"E0.bottom"),sQuery(id+"F0.wireOp",EDGE,"E0.top"),sQuery(id+"F0.wireOp",EDGE,"E0.left"),sQuery(id+"F0.wireOp",EDGE,"E0.right")])],"isStart":true}),makeQuery(id+"F31.opExtrude","CAP_FACE",FACE,{"disambiguationData":[OSD([sQuery(id+"F30.wireOp",EDGE,"E46.bottom"),sQuery(id+"F30.wireOp",EDGE,"E46.top"),sQuery(id+"F30.wireOp",EDGE,"E46.left"),sQuery(id+"F30.wireOp",EDGE,"E46.right")])],"isStart":true}),makeQuery(id+"F31.opExtrude","CAP_FACE",FACE,{"disambiguationData":[OSD([sQuery(id+"F30.wireOp",EDGE,"E48.MirrorCS"),sQuery(id+"F30.wireOp",EDGE,"E49.MirrorCS"),sQuery(id+"F30.wireOp",EDGE,"E50.MirrorCS"),sQuery(id+"F30.wireOp",EDGE,"E51.MirrorCS")])],"isStart":true})]}),makeQuery(id+"F33.opExtrude","CAP_FACE",FACE,{"disambiguationData":[OSD([sQuery(id+"F32.wireOp",EDGE,"E52.bottom"),sQuery(id+"F32.wireOp",EDGE,"E52.top"),sQuery(id+"F32.wireOp",EDGE,"E52.left"),sQuery(id+"F32.wireOp",EDGE,"E52.right")])],"isStart":true}),makeQuery(id+"F33.opExtrude","CAP_FACE",FACE,{"disambiguationData":[OSD([sQuery(id+"F32.wireOp",EDGE,"E54.MirrorCS"),sQuery(id+"F32.wireOp",EDGE,"E55.MirrorCS"),sQuery(id+"F32.wireOp",EDGE,"E56.MirrorCS"),sQuery(id+"F32.wireOp",EDGE,"E57.MirrorCS")])],"isStart":true})]});
            var sketch = newSketch(context, id + "F40", { "sketchPlane" : qUnion([Q0])});
            skLineSegment(sketch, "E65.bottom", {"start": v(-3732.4, -5867.4) * mm, "end": v(-3224.4, -5867.4) * mm});
            skLineSegment(sketch, "E65.top", {"start": v(-3732.4, -5359.4) * mm, "end": v(-3224.4, -5359.4) * mm});
            skLineSegment(sketch, "E65.left", {"start": v(-3732.4, -5867.4) * mm, "end": v(-3732.4, -5359.4) * mm});
            skLineSegment(sketch, "E65.right", {"start": v(-3224.4, -5867.4) * mm, "end": v(-3224.4, -5359.4) * mm});
            skSolve(sketch);
        }
        {
            var Q0;
            Q0 = qSketchRegion(id + "F40", true);
            extrude(context, id + "F41", {"entities" : qUnion([Q0]), "operationType" : NewBodyOperationType.ADD, "oppositeDirection" : true, "depth" : 8890 * mm});
        }
        {
            var Q0;
            Q0=makeQuery(id+"F41.opExtrude","CAP_FACE",FACE,{"disambiguationData":[OSD([sQuery(id+"F40.wireOp",EDGE,"E65.bottom"),sQuery(id+"F40.wireOp",EDGE,"E65.top"),sQuery(id+"F40.wireOp",EDGE,"E65.left"),sQuery(id+"F40.wireOp",EDGE,"E65.right")])],"isStart":false});
            var sketch = newSketch(context, id + "F42", { "sketchPlane" : qUnion([Q0])});
            skLineSegment(sketch, "E66.0", {"start": v(-3770.5, 5905.5) * mm, "end": v(-3770.5, 5321.3) * mm});
            skLineSegment(sketch, "E66.1", {"start": v(-3186.3, 5905.5) * mm, "end": v(-3770.5, 5905.5) * mm});
            skLineSegment(sketch, "E66.2", {"start": v(-3186.3, 5321.3) * mm, "end": v(-3186.3, 5905.5) * mm});
            skLineSegment(sketch, "E66.3", {"start": v(-3770.5, 5321.3) * mm, "end": v(-3186.3, 5321.3) * mm});
            skSolve(sketch);
        }
        {
            var Q0;
            Q0 = qSketchRegion(id + "F42", true);
            extrude(context, id + "F43", {"entities" : qUnion([Q0]), "operationType" : NewBodyOperationType.ADD, "depth" : 50.8 * mm});
        }
        {
            var Q0;
            Q0=makeQuery(id+"F43.opExtrude","CAP_FACE",FACE,{"disambiguationData":[OSD([sQuery(id+"F42.wireOp",EDGE,"E66.0"),sQuery(id+"F42.wireOp",EDGE,"E66.1"),sQuery(id+"F42.wireOp",EDGE,"E66.2"),sQuery(id+"F42.wireOp",EDGE,"E66.3")])],"isStart":false});
            var sketch = newSketch(context, id + "F44", { "sketchPlane" : qUnion([Q0])});
            skLineSegment(sketch, "E67.0", {"start": v(-3224.4, 5867.4) * mm, "end": v(-3732.4, 5867.4) * mm});
            skLineSegment(sketch, "E67.1", {"start": v(-3224.4, 5359.4) * mm, "end": v(-3224.4, 5867.4) * mm});
            skLineSegment(sketch, "E67.2", {"start": v(-3732.4, 5359.4) * mm, "end": v(-3224.4, 5359.4) * mm});
            skLineSegment(sketch, "E67.3", {"start": v(-3732.4, 5867.4) * mm, "end": v(-3732.4, 5359.4) * mm});
            skSolve(sketch);
        }
        {
            var Q0;
            Q0 = qSketchRegion(id + "F44", true);
            extrude(context, id + "F45", {"entities" : qUnion([Q0]), "operationType" : NewBodyOperationType.ADD, "depth" : 203.2 * mm});
        }
        {
            var Q0;
            Q0=makeQuery(id+"F45.opExtrude","CAP_FACE",FACE,{"disambiguationData":[OSD([sQuery(id+"F44.wireOp",EDGE,"E67.0"),sQuery(id+"F44.wireOp",EDGE,"E67.1"),sQuery(id+"F44.wireOp",EDGE,"E67.2"),sQuery(id+"F44.wireOp",EDGE,"E67.3")])],"isStart":false});
            var sketch = newSketch(context, id + "F46", { "sketchPlane" : qUnion([Q0])});
            skLineSegment(sketch, "E68.0.0", {"start": v(-3224.4, 5359.4) * mm, "end": v(-3224.4, 5867.4) * mm});
            skLineSegment(sketch, "E68.0.1", {"start": v(-3224.4, 5867.4) * mm, "end": v(-3732.4, 5867.4) * mm});
            skLineSegment(sketch, "E68.0.2", {"start": v(-3732.4, 5867.4) * mm, "end": v(-3732.4, 5359.4) * mm});
            skLineSegment(sketch, "E68.0.3", {"start": v(-3732.4, 5359.4) * mm, "end": v(-3224.4, 5359.4) * mm});
            skSolve(sketch);
        }
        {
            var Q0;
            Q0 = qSketchRegion(id + "F46", true);
            extrude(context, id + "F47", {"entities" : qUnion([Q0]), "operationType" : NewBodyOperationType.ADD, "depth" : 355.6 * mm, "hasDraft" : true, "draftAngle" : 10 * degree});
        }
        {
            var Q0;
            Q0=makeQuery(id+"F47.opExtrude","CAP_FACE",FACE,{"disambiguationData":[OSD([sQuery(id+"F46.wireOp",EDGE,"E68.0.0"),sQuery(id+"F46.wireOp",EDGE,"E68.0.1"),sQuery(id+"F46.wireOp",EDGE,"E68.0.2"),sQuery(id+"F46.wireOp",EDGE,"E68.0.3")])],"isStart":false});
            var sketch = newSketch(context, id + "F48", { "sketchPlane" : qUnion([Q0])});
            skLineSegment(sketch, "E69.0", {"start": v(-3744.3, 5347.5) * mm, "end": v(-3212.5, 5347.5) * mm});
            skLineSegment(sketch, "E69.1", {"start": v(-3744.3, 5879.3) * mm, "end": v(-3744.3, 5347.5) * mm});
            skLineSegment(sketch, "E69.2", {"start": v(-3212.5, 5879.3) * mm, "end": v(-3744.3, 5879.3) * mm});
            skLineSegment(sketch, "E69.3", {"start": v(-3212.5, 5347.5) * mm, "end": v(-3212.5, 5879.3) * mm});
            skSolve(sketch);
        }
        {
            var Q0;
            Q0 = qSketchRegion(id + "F48", true);
            extrude(context, id + "F49", {"entities" : qUnion([Q0]), "operationType" : NewBodyOperationType.ADD, "depth" : 50.8 * mm});
        }
        {
            var Q0;
            Q0=makeQuery(id+"F49.opExtrude","CAP_FACE",FACE,{"disambiguationData":[OSD([sQuery(id+"F48.wireOp",EDGE,"E69.0"),sQuery(id+"F48.wireOp",EDGE,"E69.1"),sQuery(id+"F48.wireOp",EDGE,"E69.2"),sQuery(id+"F48.wireOp",EDGE,"E69.3")])],"isStart":false});
            var sketch = newSketch(context, id + "F50", { "sketchPlane" : qUnion([Q0])});
            skLineSegment(sketch, "E70.0", {"start": v(-3693.5, 5828.5) * mm, "end": v(-3693.5, 5398.3) * mm});
            skLineSegment(sketch, "E70.1", {"start": v(-3263.3, 5828.5) * mm, "end": v(-3693.5, 5828.5) * mm});
            skLineSegment(sketch, "E70.2", {"start": v(-3263.3, 5398.3) * mm, "end": v(-3263.3, 5828.5) * mm});
            skLineSegment(sketch, "E70.3", {"start": v(-3693.5, 5398.3) * mm, "end": v(-3263.3, 5398.3) * mm});
            skSolve(sketch);
        }
        {
            var Q0;
            Q0 = qSketchRegion(id + "F50", true);
            extrude(context, id + "F51", {"entities" : qUnion([Q0]), "operationType" : NewBodyOperationType.REMOVE, "oppositeDirection" : true, "depth" : 508 * mm});
        }
        {
            var Q0;
            Q0=makeQuery(id+"F33.boolean.opBoolean","MERGE",FACE,{"derivedFrom":[makeQuery(id+"F31.boolean.opBoolean","MERGE",FACE,{"derivedFrom":[makeQuery(id+"F1.opExtrude","CAP_FACE",FACE,{"disambiguationData":[OSD([sQuery(id+"F0.wireOp",EDGE,"E0.bottom"),sQuery(id+"F0.wireOp",EDGE,"E0.top"),sQuery(id+"F0.wireOp",EDGE,"E0.left"),sQuery(id+"F0.wireOp",EDGE,"E0.right")])],"isStart":true}),makeQuery(id+"F31.opExtrude","CAP_FACE",FACE,{"disambiguationData":[OSD([sQuery(id+"F30.wireOp",EDGE,"E46.bottom"),sQuery(id+"F30.wireOp",EDGE,"E46.top"),sQuery(id+"F30.wireOp",EDGE,"E46.left"),sQuery(id+"F30.wireOp",EDGE,"E46.right")])],"isStart":true}),makeQuery(id+"F31.opExtrude","CAP_FACE",FACE,{"disambiguationData":[OSD([sQuery(id+"F30.wireOp",EDGE,"E48.MirrorCS"),sQuery(id+"F30.wireOp",EDGE,"E49.MirrorCS"),sQuery(id+"F30.wireOp",EDGE,"E50.MirrorCS"),sQuery(id+"F30.wireOp",EDGE,"E51.MirrorCS")])],"isStart":true})]}),makeQuery(id+"F33.opExtrude","CAP_FACE",FACE,{"disambiguationData":[OSD([sQuery(id+"F32.wireOp",EDGE,"E52.bottom"),sQuery(id+"F32.wireOp",EDGE,"E52.top"),sQuery(id+"F32.wireOp",EDGE,"E52.left"),sQuery(id+"F32.wireOp",EDGE,"E52.right")])],"isStart":true}),makeQuery(id+"F33.opExtrude","CAP_FACE",FACE,{"disambiguationData":[OSD([sQuery(id+"F32.wireOp",EDGE,"E54.MirrorCS"),sQuery(id+"F32.wireOp",EDGE,"E55.MirrorCS"),sQuery(id+"F32.wireOp",EDGE,"E56.MirrorCS"),sQuery(id+"F32.wireOp",EDGE,"E57.MirrorCS")])],"isStart":true})]});
            var sketch = newSketch(context, id + "F52", { "sketchPlane" : qUnion([Q0])});
            skLineSegment(sketch, "E71.0", {"start": v(-6604, -14757.4) * mm, "end": v(-381, -14757.4) * mm});
            skLineSegment(sketch, "E71.1", {"start": v(-6604, -381) * mm, "end": v(-6604, -14757.4) * mm});
            skLineSegment(sketch, "E71.2", {"start": v(-381, -381) * mm, "end": v(-6604, -381) * mm});
            skLineSegment(sketch, "E71.3", {"start": v(-381, -14757.4) * mm, "end": v(-381, -381) * mm});
            skSolve(sketch);
        }
        {
            var Q0;
            Q0 = qSketchRegion(id + "F52", true);
            extrude(context, id + "F53", {"entities" : qUnion([Q0]), "operationType" : NewBodyOperationType.ADD, "depth" : 2032 * mm});
        }
        {
            var Q0;
            Q0=makeQuery(id+"F21.boolean.opBoolean","SPLIT",FACE,{"disambiguationData":[TD([makeQuery(id+"F1.opExtrude","CAP_FACE",FACE,{"disambiguationData":[OSD([sQuery(id+"F0.wireOp",EDGE,"E0.bottom"),sQuery(id+"F0.wireOp",EDGE,"E0.top"),sQuery(id+"F0.wireOp",EDGE,"E0.left"),sQuery(id+"F0.wireOp",EDGE,"E0.right")])],"isStart":true})])],"derivedFrom":makeQuery(id+"F18.boolean.opBoolean","MERGE",FACE,{"derivedFrom":[makeQuery(id+"F10.boolean.opBoolean","COPY",FACE,{"derivedFrom":makeQuery(id+"F10.opExtrude","CAP_FACE",FACE,{"disambiguationData":[OSD([sQuery(id+"F9.wireOp",EDGE,"E10"),sQuery(id+"F9.wireOp",EDGE,"E11"),sQuery(id+"F9.wireOp",EDGE,"E12"),sQuery(id+"F9.wireOp",EDGE,"E13"),sQuery(id+"F9.wireOp",EDGE,"E14"),sQuery(id+"F9.wireOp",EDGE,"E15"),sQuery(id+"F9.wireOp",EDGE,"E16"),sQuery(id+"F9.wireOp",EDGE,"E17")])],"isStart":false})}),makeQuery(id+"F18.opExtrude","SWEPT_FACE",FACE,{"disambiguationData":[OSD([sQuery(id+"F17.wireOp",EDGE,"E32.right")])]})]})});
            var sketch = newSketch(context, id + "F54", { "sketchPlane" : qUnion([Q0])});
            skLineSegment(sketch, "E72.bottom", {"start": v(1143, 2184.4) * mm, "end": v(2006.6, 2184.4) * mm});
            skLineSegment(sketch, "E72.top", {"start": v(1143, 965.2) * mm, "end": v(2006.6, 965.2) * mm});
            skLineSegment(sketch, "E72.left", {"start": v(1143, 2184.4) * mm, "end": v(1143, 965.2) * mm});
            skLineSegment(sketch, "E72.right", {"start": v(2006.6, 2184.4) * mm, "end": v(2006.6, 965.2) * mm});
            skLineSegment(sketch, "E73.bottom", {"start": v(2616.2, 2184.4) * mm, "end": v(3479.8, 2184.4) * mm});
            skLineSegment(sketch, "E73.top", {"start": v(2616.2, 965.2) * mm, "end": v(3479.8, 965.2) * mm});
            skLineSegment(sketch, "E73.left", {"start": v(2616.2, 2184.4) * mm, "end": v(2616.2, 965.2) * mm});
            skLineSegment(sketch, "E73.right", {"start": v(3479.8, 2184.4) * mm, "end": v(3479.8, 965.2) * mm});
            skLineSegment(sketch, "E74.bottom", {"start": v(6019.8, 2184.4) * mm, "end": v(6883.4, 2184.4) * mm});
            skLineSegment(sketch, "E74.top", {"start": v(6019.8, 965.2) * mm, "end": v(6883.4, 965.2) * mm});
            skLineSegment(sketch, "E74.left", {"start": v(6019.8, 2184.4) * mm, "end": v(6019.8, 965.2) * mm});
            skLineSegment(sketch, "E74.right", {"start": v(6883.4, 2184.4) * mm, "end": v(6883.4, 965.2) * mm});
            skLineSegment(sketch, "E75.bottom", {"start": v(7442.2, 2184.4) * mm, "end": v(8305.8, 2184.4) * mm});
            skLineSegment(sketch, "E75.top", {"start": v(7442.2, 965.2) * mm, "end": v(8305.8, 965.2) * mm});
            skLineSegment(sketch, "E75.left", {"start": v(7442.2, 2184.4) * mm, "end": v(7442.2, 965.2) * mm});
            skLineSegment(sketch, "E75.right", {"start": v(8305.8, 2184.4) * mm, "end": v(8305.8, 965.2) * mm});
            skLineSegment(sketch, "E76.bottom", {"start": v(10896.6, 2184.4) * mm, "end": v(11760.2, 2184.4) * mm});
            skLineSegment(sketch, "E76.top", {"start": v(10896.6, 965.2) * mm, "end": v(11760.2, 965.2) * mm});
            skLineSegment(sketch, "E76.left", {"start": v(10896.6, 2184.4) * mm, "end": v(10896.6, 965.2) * mm});
            skLineSegment(sketch, "E76.right", {"start": v(11760.2, 2184.4) * mm, "end": v(11760.2, 965.2) * mm});
            skLineSegment(sketch, "E77.bottom", {"start": v(13081, 2184.4) * mm, "end": v(13944.6, 2184.4) * mm});
            skLineSegment(sketch, "E77.top", {"start": v(13081, 965.2) * mm, "end": v(13944.6, 965.2) * mm});
            skLineSegment(sketch, "E77.left", {"start": v(13081, 2184.4) * mm, "end": v(13081, 965.2) * mm});
            skLineSegment(sketch, "E77.right", {"start": v(13944.6, 2184.4) * mm, "end": v(13944.6, 965.2) * mm});
            skLineSegment(sketch, "E78.bottom", {"start": v(4191, 2387.6) * mm, "end": v(5105.4, 2387.6) * mm});
            skLineSegment(sketch, "E78.top", {"start": v(4191, 254) * mm, "end": v(5105.4, 254) * mm});
            skLineSegment(sketch, "E78.left", {"start": v(4191, 2387.6) * mm, "end": v(4191, 254) * mm});
            skLineSegment(sketch, "E78.right", {"start": v(5105.4, 2387.6) * mm, "end": v(5105.4, 254) * mm});
            skLineSegment(sketch, "E79.bottom", {"start": v(9220.2, 2387.6) * mm, "end": v(10134.6, 2387.6) * mm});
            skLineSegment(sketch, "E79.top", {"start": v(9220.2, 254) * mm, "end": v(10134.6, 254) * mm});
            skLineSegment(sketch, "E79.left", {"start": v(9220.2, 2387.6) * mm, "end": v(9220.2, 254) * mm});
            skLineSegment(sketch, "E79.right", {"start": v(10134.6, 2387.6) * mm, "end": v(10134.6, 254) * mm});
            skLineSegment(sketch, "E80.bottom", {"start": v(1701.8, 4546.6) * mm, "end": v(2565.4, 4546.6) * mm});
            skLineSegment(sketch, "E80.top", {"start": v(1701.8, 3327.4) * mm, "end": v(2565.4, 3327.4) * mm});
            skLineSegment(sketch, "E80.left", {"start": v(1701.8, 4546.6) * mm, "end": v(1701.8, 3327.4) * mm});
            skLineSegment(sketch, "E80.right", {"start": v(2565.4, 4546.6) * mm, "end": v(2565.4, 3327.4) * mm});
            skLineSegment(sketch, "E81.bottom", {"start": v(4216.4, 4546.6) * mm, "end": v(5080, 4546.6) * mm});
            skLineSegment(sketch, "E81.top", {"start": v(4216.4, 3327.4) * mm, "end": v(5080, 3327.4) * mm});
            skLineSegment(sketch, "E81.left", {"start": v(4216.4, 4546.6) * mm, "end": v(4216.4, 3327.4) * mm});
            skLineSegment(sketch, "E81.right", {"start": v(5080, 4546.6) * mm, "end": v(5080, 3327.4) * mm});
            skLineSegment(sketch, "E82.bottom", {"start": v(6744.89, 4546.6) * mm, "end": v(7608.49, 4546.6) * mm});
            skLineSegment(sketch, "E82.top", {"start": v(6744.89, 3327.4) * mm, "end": v(7608.49, 3327.4) * mm});
            skLineSegment(sketch, "E82.left", {"start": v(6744.89, 4546.6) * mm, "end": v(6744.89, 3327.4) * mm});
            skLineSegment(sketch, "E82.right", {"start": v(7608.49, 4546.6) * mm, "end": v(7608.49, 3327.4) * mm});
            skLineSegment(sketch, "E83.bottom", {"start": v(9906, 4546.6) * mm, "end": v(10769.6, 4546.6) * mm});
            skLineSegment(sketch, "E83.top", {"start": v(9906, 3327.4) * mm, "end": v(10769.6, 3327.4) * mm});
            skLineSegment(sketch, "E83.left", {"start": v(9906, 4546.6) * mm, "end": v(9906, 3327.4) * mm});
            skLineSegment(sketch, "E83.right", {"start": v(10769.6, 4546.6) * mm, "end": v(10769.6, 3327.4) * mm});
            skLineSegment(sketch, "E84.bottom", {"start": v(12725.4, 4546.6) * mm, "end": v(13589, 4546.6) * mm});
            skLineSegment(sketch, "E84.top", {"start": v(12725.4, 3327.4) * mm, "end": v(13589, 3327.4) * mm});
            skLineSegment(sketch, "E84.left", {"start": v(12725.4, 4546.6) * mm, "end": v(12725.4, 3327.4) * mm});
            skLineSegment(sketch, "E84.right", {"start": v(13589, 4546.6) * mm, "end": v(13589, 3327.4) * mm});
            skLineSegment(sketch, "E85.bottom", {"start": v(11328.4, 6192.25) * mm, "end": v(12039.6, 6192.25) * mm});
            skLineSegment(sketch, "E85.top", {"start": v(11328.4, 5176.25) * mm, "end": v(12039.6, 5176.25) * mm});
            skLineSegment(sketch, "E85.left", {"start": v(11328.4, 6192.25) * mm, "end": v(11328.4, 5176.25) * mm});
            skLineSegment(sketch, "E85.right", {"start": v(12039.6, 6192.25) * mm, "end": v(12039.6, 5176.25) * mm});
            skSolve(sketch);
        }
        {
            var Q0;
            Q0 = qSketchRegion(id + "F54", true);
            extrude(context, id + "F55", {"entities" : qUnion([Q0]), "operationType" : NewBodyOperationType.ADD, "depth" : 25.4 * mm, "hasSecondDirection" : true, "secondDirectionOppositeDirection" : true, "secondDirectionDepth" : 6400.8 * mm});
        }
        {
            var Q0;
            Q0=makeQuery(id+"F55.opExtrude","CAP_FACE",FACE,{"disambiguationData":[OSD([sQuery(id+"F54.wireOp",EDGE,"E72.bottom"),sQuery(id+"F54.wireOp",EDGE,"E72.top"),sQuery(id+"F54.wireOp",EDGE,"E72.left"),sQuery(id+"F54.wireOp",EDGE,"E72.right")])],"isStart":false});
            var sketch = newSketch(context, id + "F56", { "sketchPlane" : qUnion([Q0])});
            skLineSegment(sketch, "E86.0", {"start": v(1905, 2082.8) * mm, "end": v(1244.6, 2082.8) * mm});
            skLineSegment(sketch, "E86.1", {"start": v(1905, 1066.8) * mm, "end": v(1905, 2082.8) * mm});
            skLineSegment(sketch, "E86.2", {"start": v(1244.6, 1066.8) * mm, "end": v(1905, 1066.8) * mm});
            skLineSegment(sketch, "E86.3", {"start": v(1244.6, 2082.8) * mm, "end": v(1244.6, 1066.8) * mm});
            skLineSegment(sketch, "E87.0", {"start": v(3378.2, 2082.8) * mm, "end": v(2717.8, 2082.8) * mm});
            skLineSegment(sketch, "E87.1", {"start": v(3378.2, 1066.8) * mm, "end": v(3378.2, 2082.8) * mm});
            skLineSegment(sketch, "E87.2", {"start": v(2717.8, 1066.8) * mm, "end": v(3378.2, 1066.8) * mm});
            skLineSegment(sketch, "E87.3", {"start": v(2717.8, 2082.8) * mm, "end": v(2717.8, 1066.8) * mm});
            skLineSegment(sketch, "E88.0", {"start": v(6781.8, 2082.8) * mm, "end": v(6121.4, 2082.8) * mm});
            skLineSegment(sketch, "E88.1", {"start": v(6781.8, 1066.8) * mm, "end": v(6781.8, 2082.8) * mm});
            skLineSegment(sketch, "E88.2", {"start": v(6121.4, 1066.8) * mm, "end": v(6781.8, 1066.8) * mm});
            skLineSegment(sketch, "E88.3", {"start": v(6121.4, 2082.8) * mm, "end": v(6121.4, 1066.8) * mm});
            skLineSegment(sketch, "E89.0", {"start": v(8204.2, 2082.8) * mm, "end": v(7543.8, 2082.8) * mm});
            skLineSegment(sketch, "E89.1", {"start": v(8204.2, 1066.8) * mm, "end": v(8204.2, 2082.8) * mm});
            skLineSegment(sketch, "E89.2", {"start": v(7543.8, 1066.8) * mm, "end": v(8204.2, 1066.8) * mm});
            skLineSegment(sketch, "E89.3", {"start": v(7543.8, 2082.8) * mm, "end": v(7543.8, 1066.8) * mm});
            skLineSegment(sketch, "E90.0", {"start": v(11658.6, 2082.8) * mm, "end": v(10998.2, 2082.8) * mm});
            skLineSegment(sketch, "E90.1", {"start": v(11658.6, 1066.8) * mm, "end": v(11658.6, 2082.8) * mm});
            skLineSegment(sketch, "E90.2", {"start": v(10998.2, 1066.8) * mm, "end": v(11658.6, 1066.8) * mm});
            skLineSegment(sketch, "E90.3", {"start": v(10998.2, 2082.8) * mm, "end": v(10998.2, 1066.8) * mm});
            skLineSegment(sketch, "E91.0", {"start": v(13843, 2082.8) * mm, "end": v(13182.6, 2082.8) * mm});
            skLineSegment(sketch, "E91.1", {"start": v(13843, 1066.8) * mm, "end": v(13843, 2082.8) * mm});
            skLineSegment(sketch, "E91.2", {"start": v(13182.6, 1066.8) * mm, "end": v(13843, 1066.8) * mm});
            skLineSegment(sketch, "E91.3", {"start": v(13182.6, 2082.8) * mm, "end": v(13182.6, 1066.8) * mm});
            skLineSegment(sketch, "E92.0", {"start": v(2463.8, 4445) * mm, "end": v(1803.4, 4445) * mm});
            skLineSegment(sketch, "E92.1", {"start": v(2463.8, 3429) * mm, "end": v(2463.8, 4445) * mm});
            skLineSegment(sketch, "E92.2", {"start": v(1803.4, 3429) * mm, "end": v(2463.8, 3429) * mm});
            skLineSegment(sketch, "E92.3", {"start": v(1803.4, 4445) * mm, "end": v(1803.4, 3429) * mm});
            skLineSegment(sketch, "E93.0", {"start": v(4978.4, 4445) * mm, "end": v(4318, 4445) * mm});
            skLineSegment(sketch, "E93.1", {"start": v(4978.4, 3429) * mm, "end": v(4978.4, 4445) * mm});
            skLineSegment(sketch, "E93.2", {"start": v(4318, 3429) * mm, "end": v(4978.4, 3429) * mm});
            skLineSegment(sketch, "E93.3", {"start": v(4318, 4445) * mm, "end": v(4318, 3429) * mm});
            skLineSegment(sketch, "E94.0", {"start": v(7506.89, 4445) * mm, "end": v(6846.49, 4445) * mm});
            skLineSegment(sketch, "E94.1", {"start": v(7506.89, 3429) * mm, "end": v(7506.89, 4445) * mm});
            skLineSegment(sketch, "E94.2", {"start": v(6846.49, 3429) * mm, "end": v(7506.89, 3429) * mm});
            skLineSegment(sketch, "E94.3", {"start": v(6846.49, 4445) * mm, "end": v(6846.49, 3429) * mm});
            skLineSegment(sketch, "E95.0", {"start": v(10668, 4445) * mm, "end": v(10007.6, 4445) * mm});
            skLineSegment(sketch, "E95.1", {"start": v(10668, 3429) * mm, "end": v(10668, 4445) * mm});
            skLineSegment(sketch, "E95.2", {"start": v(10007.6, 3429) * mm, "end": v(10668, 3429) * mm});
            skLineSegment(sketch, "E95.3", {"start": v(10007.6, 4445) * mm, "end": v(10007.6, 3429) * mm});
            skLineSegment(sketch, "E96.0", {"start": v(13487.4, 4445) * mm, "end": v(12827, 4445) * mm});
            skLineSegment(sketch, "E96.1", {"start": v(13487.4, 3429) * mm, "end": v(13487.4, 4445) * mm});
            skLineSegment(sketch, "E96.2", {"start": v(12827, 3429) * mm, "end": v(13487.4, 3429) * mm});
            skLineSegment(sketch, "E96.3", {"start": v(12827, 4445) * mm, "end": v(12827, 3429) * mm});
            skLineSegment(sketch, "E97.0", {"start": v(11963.4, 6116.05) * mm, "end": v(11404.6, 6116.05) * mm});
            skLineSegment(sketch, "E97.1", {"start": v(11963.4, 5252.45) * mm, "end": v(11963.4, 6116.05) * mm});
            skLineSegment(sketch, "E97.2", {"start": v(11404.6, 5252.45) * mm, "end": v(11963.4, 5252.45) * mm});
            skLineSegment(sketch, "E97.3", {"start": v(11404.6, 6116.05) * mm, "end": v(11404.6, 5252.45) * mm});
            skLineSegment(sketch, "E98.0", {"start": v(5029.2, 2311.4) * mm, "end": v(4267.2, 2311.4) * mm});
            skLineSegment(sketch, "E98.1", {"start": v(5029.2, 330.2) * mm, "end": v(5029.2, 2311.4) * mm});
            skLineSegment(sketch, "E98.2", {"start": v(4267.2, 330.2) * mm, "end": v(5029.2, 330.2) * mm});
            skLineSegment(sketch, "E98.3", {"start": v(4267.2, 2311.4) * mm, "end": v(4267.2, 330.2) * mm});
            skLineSegment(sketch, "E99.0", {"start": v(10058.4, 2311.4) * mm, "end": v(9296.4, 2311.4) * mm});
            skLineSegment(sketch, "E99.1", {"start": v(10058.4, 330.2) * mm, "end": v(10058.4, 2311.4) * mm});
            skLineSegment(sketch, "E99.2", {"start": v(9296.4, 330.2) * mm, "end": v(10058.4, 330.2) * mm});
            skLineSegment(sketch, "E99.3", {"start": v(9296.4, 2311.4) * mm, "end": v(9296.4, 330.2) * mm});
            skSolve(sketch);
        }
        {
            var Q0;
            Q0 = qSketchRegion(id + "F56", true);
            extrude(context, id + "F57", {"entities" : qUnion([Q0]), "operationType" : NewBodyOperationType.REMOVE, "oppositeDirection" : true, "depth" : 50.8 * mm});
        }
        {
            var Q0;
            Q0=makeQuery(id+"F21.boolean.opBoolean","SPLIT",FACE,{"disambiguationData":[TD([makeQuery(id+"F1.opExtrude","CAP_FACE",FACE,{"disambiguationData":[OSD([sQuery(id+"F0.wireOp",EDGE,"E0.bottom"),sQuery(id+"F0.wireOp",EDGE,"E0.top"),sQuery(id+"F0.wireOp",EDGE,"E0.left"),sQuery(id+"F0.wireOp",EDGE,"E0.right")])],"isStart":true})])],"derivedFrom":makeQuery(id+"F16.boolean.opBoolean","COPY",FACE,{"derivedFrom":makeQuery(id+"F16.opExtrude","CAP_FACE",FACE,{"disambiguationData":[OSD([sQuery(id+"F15.wireOp",EDGE,"E20"),sQuery(id+"F15.wireOp",EDGE,"E21"),sQuery(id+"F15.wireOp",EDGE,"E22"),sQuery(id+"F15.wireOp",EDGE,"E23"),sQuery(id+"F15.wireOp",EDGE,"E24"),sQuery(id+"F15.wireOp",EDGE,"E25"),sQuery(id+"F15.wireOp",EDGE,"E26.MirrorCS"),sQuery(id+"F15.wireOp",EDGE,"E27.MirrorCS"),sQuery(id+"F15.wireOp",EDGE,"E28.MirrorCS"),sQuery(id+"F15.wireOp",EDGE,"E29.MirrorCS"),sQuery(id+"F15.wireOp",EDGE,"E30.MirrorCS"),sQuery(id+"F15.wireOp",EDGE,"E31.MirrorCS")])],"isStart":false})})});
            var sketch = newSketch(context, id + "F58", { "sketchPlane" : qUnion([Q0])});
            skLineSegment(sketch, "E100.bottom", {"start": v(-5283.2, 2184.4) * mm, "end": v(-4419.6, 2184.4) * mm});
            skLineSegment(sketch, "E100.top", {"start": v(-5283.2, 965.2) * mm, "end": v(-4419.6, 965.2) * mm});
            skLineSegment(sketch, "E100.left", {"start": v(-5283.2, 2184.4) * mm, "end": v(-5283.2, 965.2) * mm});
            skLineSegment(sketch, "E100.right", {"start": v(-4419.6, 2184.4) * mm, "end": v(-4419.6, 965.2) * mm});
            skLineSegment(sketch, "E101.bottom", {"start": v(-2565.4, 2184.4) * mm, "end": v(-1701.8, 2184.4) * mm});
            skLineSegment(sketch, "E101.top", {"start": v(-2565.4, 965.2) * mm, "end": v(-1701.8, 965.2) * mm});
            skLineSegment(sketch, "E101.left", {"start": v(-2565.4, 2184.4) * mm, "end": v(-2565.4, 965.2) * mm});
            skLineSegment(sketch, "E101.right", {"start": v(-1701.8, 2184.4) * mm, "end": v(-1701.8, 965.2) * mm});
            skLineSegment(sketch, "E102.bottom", {"start": v(-5283.2, 4546.6) * mm, "end": v(-4419.6, 4546.6) * mm});
            skLineSegment(sketch, "E102.top", {"start": v(-5283.2, 3327.4) * mm, "end": v(-4419.6, 3327.4) * mm});
            skLineSegment(sketch, "E102.left", {"start": v(-5283.2, 4546.6) * mm, "end": v(-5283.2, 3327.4) * mm});
            skLineSegment(sketch, "E102.right", {"start": v(-4419.6, 4546.6) * mm, "end": v(-4419.6, 3327.4) * mm});
            skLineSegment(sketch, "E103.bottom", {"start": v(-2565.4, 4546.6) * mm, "end": v(-1701.8, 4546.6) * mm});
            skLineSegment(sketch, "E103.top", {"start": v(-2565.4, 3327.4) * mm, "end": v(-1701.8, 3327.4) * mm});
            skLineSegment(sketch, "E103.left", {"start": v(-2565.4, 4546.6) * mm, "end": v(-2565.4, 3327.4) * mm});
            skLineSegment(sketch, "E103.right", {"start": v(-1701.8, 4546.6) * mm, "end": v(-1701.8, 3327.4) * mm});
            skLineSegment(sketch, "E104.bottom", {"start": v(-3911.6, 7121.09) * mm, "end": v(-3048, 7121.09) * mm});
            skLineSegment(sketch, "E104.top", {"start": v(-3911.6, 5901.89) * mm, "end": v(-3048, 5901.89) * mm});
            skLineSegment(sketch, "E104.left", {"start": v(-3911.6, 7121.09) * mm, "end": v(-3911.6, 5901.89) * mm});
            skLineSegment(sketch, "E104.right", {"start": v(-3048, 7121.09) * mm, "end": v(-3048, 5901.89) * mm});
            skSolve(sketch);
        }
        {
            var Q0;
            Q0 = qSketchRegion(id + "F58", true);
            extrude(context, id + "F59", {"entities" : qUnion([Q0]), "operationType" : NewBodyOperationType.ADD, "depth" : 25.4 * mm});
        }
        {
            var Q0;
            Q0=makeQuery(id+"F59.opExtrude","CAP_FACE",FACE,{"disambiguationData":[OSD([sQuery(id+"F58.wireOp",EDGE,"E104.bottom"),sQuery(id+"F58.wireOp",EDGE,"E104.top"),sQuery(id+"F58.wireOp",EDGE,"E104.left"),sQuery(id+"F58.wireOp",EDGE,"E104.right")])],"isStart":false});
            var sketch = newSketch(context, id + "F60", { "sketchPlane" : qUnion([Q0])});
            skLineSegment(sketch, "E105.0", {"start": v(-3149.6, 7019.49) * mm, "end": v(-3810, 7019.49) * mm});
            skLineSegment(sketch, "E105.1", {"start": v(-3149.6, 6003.49) * mm, "end": v(-3149.6, 7019.49) * mm});
            skLineSegment(sketch, "E105.2", {"start": v(-3810, 6003.49) * mm, "end": v(-3149.6, 6003.49) * mm});
            skLineSegment(sketch, "E105.3", {"start": v(-3810, 7019.49) * mm, "end": v(-3810, 6003.49) * mm});
            skLineSegment(sketch, "E106.0", {"start": v(-4521.2, 4445) * mm, "end": v(-5181.6, 4445) * mm});
            skLineSegment(sketch, "E106.1", {"start": v(-4521.2, 3429) * mm, "end": v(-4521.2, 4445) * mm});
            skLineSegment(sketch, "E106.2", {"start": v(-5181.6, 3429) * mm, "end": v(-4521.2, 3429) * mm});
            skLineSegment(sketch, "E106.3", {"start": v(-5181.6, 4445) * mm, "end": v(-5181.6, 3429) * mm});
            skLineSegment(sketch, "E107.0", {"start": v(-1803.4, 4445) * mm, "end": v(-2463.8, 4445) * mm});
            skLineSegment(sketch, "E107.1", {"start": v(-1803.4, 3429) * mm, "end": v(-1803.4, 4445) * mm});
            skLineSegment(sketch, "E107.2", {"start": v(-2463.8, 3429) * mm, "end": v(-1803.4, 3429) * mm});
            skLineSegment(sketch, "E107.3", {"start": v(-2463.8, 4445) * mm, "end": v(-2463.8, 3429) * mm});
            skLineSegment(sketch, "E108.0", {"start": v(-1803.4, 2082.8) * mm, "end": v(-2463.8, 2082.8) * mm});
            skLineSegment(sketch, "E108.1", {"start": v(-1803.4, 1066.8) * mm, "end": v(-1803.4, 2082.8) * mm});
            skLineSegment(sketch, "E108.2", {"start": v(-2463.8, 1066.8) * mm, "end": v(-1803.4, 1066.8) * mm});
            skLineSegment(sketch, "E108.3", {"start": v(-2463.8, 2082.8) * mm, "end": v(-2463.8, 1066.8) * mm});
            skLineSegment(sketch, "E109.0", {"start": v(-4521.2, 2082.8) * mm, "end": v(-5181.6, 2082.8) * mm});
            skLineSegment(sketch, "E109.1", {"start": v(-4521.2, 1066.8) * mm, "end": v(-4521.2, 2082.8) * mm});
            skLineSegment(sketch, "E109.2", {"start": v(-5181.6, 1066.8) * mm, "end": v(-4521.2, 1066.8) * mm});
            skLineSegment(sketch, "E109.3", {"start": v(-5181.6, 2082.8) * mm, "end": v(-5181.6, 1066.8) * mm});
            skSolve(sketch);
        }
        {
            var Q0;
            Q0 = qSketchRegion(id + "F60", true);
            extrude(context, id + "F61", {"entities" : qUnion([Q0]), "operationType" : NewBodyOperationType.REMOVE, "oppositeDirection" : true, "depth" : 76.2 * mm});
        }
        {
            var Q0;
            Q0=makeQuery(id+"F57.boolean.opBoolean","COPY",FACE,{"derivedFrom":makeQuery(id+"F57.opExtrude","CAP_FACE",FACE,{"disambiguationData":[OSD([sQuery(id+"F56.wireOp",EDGE,"E98.0"),sQuery(id+"F56.wireOp",EDGE,"E98.1"),sQuery(id+"F56.wireOp",EDGE,"E98.2"),sQuery(id+"F56.wireOp",EDGE,"E98.3")])],"isStart":false})});
            var sketch = newSketch(context, id + "F62", { "sketchPlane" : qUnion([Q0])});
            skLineSegment(sketch, "E110.0.0", {"start": v(5029.2, 330.2) * mm, "end": v(5029.2, 2311.4) * mm});
            skLineSegment(sketch, "E110.0.1", {"start": v(5029.2, 2311.4) * mm, "end": v(4267.2, 2311.4) * mm});
            skLineSegment(sketch, "E110.0.2", {"start": v(4267.2, 2311.4) * mm, "end": v(4267.2, 330.2) * mm});
            skLineSegment(sketch, "E110.0.3", {"start": v(4267.2, 330.2) * mm, "end": v(5029.2, 330.2) * mm});
            skLineSegment(sketch, "E111.0.0", {"start": v(10058.4, 330.2) * mm, "end": v(10058.4, 2311.4) * mm});
            skLineSegment(sketch, "E111.0.1", {"start": v(10058.4, 2311.4) * mm, "end": v(9296.4, 2311.4) * mm});
            skLineSegment(sketch, "E111.0.2", {"start": v(9296.4, 2311.4) * mm, "end": v(9296.4, 330.2) * mm});
            skLineSegment(sketch, "E111.0.3", {"start": v(9296.4, 330.2) * mm, "end": v(10058.4, 330.2) * mm});
            skSolve(sketch);
        }
        {
            var Q0;
            Q0=makeQuery(id+"F21.boolean.opBoolean","SPLIT",FACE,{"disambiguationData":[TD([makeQuery(id+"F1.opExtrude","CAP_FACE",FACE,{"disambiguationData":[OSD([sQuery(id+"F0.wireOp",EDGE,"E0.bottom"),sQuery(id+"F0.wireOp",EDGE,"E0.top"),sQuery(id+"F0.wireOp",EDGE,"E0.left"),sQuery(id+"F0.wireOp",EDGE,"E0.right")])],"isStart":true})])],"derivedFrom":makeQuery(id+"F14.boolean.opBoolean","COPY",FACE,{"derivedFrom":makeQuery(id+"F14.opExtrude","SWEPT_FACE",FACE,{"disambiguationData":[OSD([sQuery(id+"F13.wireOp",EDGE,"E19.right")])]})})});
            var sketch = newSketch(context, id + "F63", { "sketchPlane" : qUnion([Q0])});
            skLineSegment(sketch, "E112.bottom", {"start": v(1295.4, 2184.4) * mm, "end": v(2159, 2184.4) * mm});
            skLineSegment(sketch, "E112.top", {"start": v(1295.4, 965.2) * mm, "end": v(2159, 965.2) * mm});
            skLineSegment(sketch, "E112.left", {"start": v(1295.4, 2184.4) * mm, "end": v(1295.4, 965.2) * mm});
            skLineSegment(sketch, "E112.right", {"start": v(2159, 2184.4) * mm, "end": v(2159, 965.2) * mm});
            skLineSegment(sketch, "E113.bottom", {"start": v(3035.3, 2387.6) * mm, "end": v(3949.7, 2387.6) * mm});
            skLineSegment(sketch, "E113.top", {"start": v(3035.3, 254) * mm, "end": v(3949.7, 254) * mm});
            skLineSegment(sketch, "E113.left", {"start": v(3035.3, 2387.6) * mm, "end": v(3035.3, 254) * mm});
            skLineSegment(sketch, "E113.right", {"start": v(3949.7, 2387.6) * mm, "end": v(3949.7, 254) * mm});
            skLineSegment(sketch, "E114.bottom", {"start": v(4826, 2184.4) * mm, "end": v(5689.6, 2184.4) * mm});
            skLineSegment(sketch, "E114.top", {"start": v(4826, 965.2) * mm, "end": v(5689.6, 965.2) * mm});
            skLineSegment(sketch, "E114.left", {"start": v(4826, 2184.4) * mm, "end": v(4826, 965.2) * mm});
            skLineSegment(sketch, "E114.right", {"start": v(5689.6, 2184.4) * mm, "end": v(5689.6, 965.2) * mm});
            skSolve(sketch);
        }
        {
            var Q0;
            Q0 = qSketchRegion(id + "F63", true);
            extrude(context, id + "F64", {"entities" : qUnion([Q0]), "operationType" : NewBodyOperationType.ADD, "depth" : 25.4 * mm});
        }
        {
            var Q0;
            Q0 = qSketchRegion(id + "F62", true);
            extrude(context, id + "F65", {"entities" : qUnion([Q0]), "operationType" : NewBodyOperationType.REMOVE, "oppositeDirection" : true, "depth" : 101.6 * mm});
        }
        {
            var Q0;
            Q0=makeQuery(id+"F64.opExtrude","CAP_FACE",FACE,{"disambiguationData":[OSD([sQuery(id+"F63.wireOp",EDGE,"E112.bottom"),sQuery(id+"F63.wireOp",EDGE,"E112.top"),sQuery(id+"F63.wireOp",EDGE,"E112.left"),sQuery(id+"F63.wireOp",EDGE,"E112.right")])],"isStart":false});
            var sketch = newSketch(context, id + "F66", { "sketchPlane" : qUnion([Q0])});
            skLineSegment(sketch, "E115.0", {"start": v(2057.4, 2082.8) * mm, "end": v(1397, 2082.8) * mm});
            skLineSegment(sketch, "E115.1", {"start": v(2057.4, 1066.8) * mm, "end": v(2057.4, 2082.8) * mm});
            skLineSegment(sketch, "E115.2", {"start": v(1397, 1066.8) * mm, "end": v(2057.4, 1066.8) * mm});
            skLineSegment(sketch, "E115.3", {"start": v(1397, 2082.8) * mm, "end": v(1397, 1066.8) * mm});
            skLineSegment(sketch, "E116.0", {"start": v(5588, 2082.8) * mm, "end": v(4927.6, 2082.8) * mm});
            skLineSegment(sketch, "E116.1", {"start": v(5588, 1066.8) * mm, "end": v(5588, 2082.8) * mm});
            skLineSegment(sketch, "E116.2", {"start": v(4927.6, 1066.8) * mm, "end": v(5588, 1066.8) * mm});
            skLineSegment(sketch, "E116.3", {"start": v(4927.6, 2082.8) * mm, "end": v(4927.6, 1066.8) * mm});
            skSolve(sketch);
        }
        {
            var Q0;
            Q0 = qSketchRegion(id + "F66", true);
            extrude(context, id + "F67", {"entities" : qUnion([Q0]), "operationType" : NewBodyOperationType.REMOVE, "oppositeDirection" : true, "depth" : 50.8 * mm});
        }
        {
            var Q0;
            Q0=makeQuery(id+"F64.opExtrude","CAP_FACE",FACE,{"disambiguationData":[OSD([sQuery(id+"F63.wireOp",EDGE,"E113.bottom"),sQuery(id+"F63.wireOp",EDGE,"E113.top"),sQuery(id+"F63.wireOp",EDGE,"E113.left"),sQuery(id+"F63.wireOp",EDGE,"E113.right")])],"isStart":false});
            var sketch = newSketch(context, id + "F68", { "sketchPlane" : qUnion([Q0])});
            skLineSegment(sketch, "E117.0", {"start": v(3873.5, 2311.4) * mm, "end": v(3111.5, 2311.4) * mm});
            skLineSegment(sketch, "E117.1", {"start": v(3873.5, 330.2) * mm, "end": v(3873.5, 2311.4) * mm});
            skLineSegment(sketch, "E117.2", {"start": v(3111.5, 330.2) * mm, "end": v(3873.5, 330.2) * mm});
            skLineSegment(sketch, "E117.3", {"start": v(3111.5, 2311.4) * mm, "end": v(3111.5, 330.2) * mm});
            skSolve(sketch);
        }
        {
            var Q0;
            Q0 = qSketchRegion(id + "F68", true);
            extrude(context, id + "F69", {"entities" : qUnion([Q0]), "operationType" : NewBodyOperationType.REMOVE, "oppositeDirection" : true, "depth" : 127 * mm});
        }
        {
            var Q0;
            Q0=makeQuery(id+"F55.opExtrude","CAP_FACE",FACE,{"disambiguationData":[OSD([sQuery(id+"F54.wireOp",EDGE,"E77.bottom"),sQuery(id+"F54.wireOp",EDGE,"E77.top"),sQuery(id+"F54.wireOp",EDGE,"E77.left"),sQuery(id+"F54.wireOp",EDGE,"E77.right")])],"isStart":true});
            var sketch = newSketch(context, id + "F70", { "sketchPlane" : qUnion([Q0])});
            skLineSegment(sketch, "E118.0.0", {"start": v(-13843, 1066.8) * mm, "end": v(-13843, 2082.8) * mm});
            skLineSegment(sketch, "E118.0.1", {"start": v(-13843, 2082.8) * mm, "end": v(-13182.6, 2082.8) * mm});
            skLineSegment(sketch, "E118.0.2", {"start": v(-13182.6, 2082.8) * mm, "end": v(-13182.6, 1066.8) * mm});
            skLineSegment(sketch, "E118.0.3", {"start": v(-13182.6, 1066.8) * mm, "end": v(-13843, 1066.8) * mm});
            skLineSegment(sketch, "E118.1.0", {"start": v(-11658.6, 1066.8) * mm, "end": v(-11658.6, 2082.8) * mm});
            skLineSegment(sketch, "E118.1.1", {"start": v(-11658.6, 2082.8) * mm, "end": v(-10998.2, 2082.8) * mm});
            skLineSegment(sketch, "E118.1.2", {"start": v(-10998.2, 2082.8) * mm, "end": v(-10998.2, 1066.8) * mm});
            skLineSegment(sketch, "E118.1.3", {"start": v(-10998.2, 1066.8) * mm, "end": v(-11658.6, 1066.8) * mm});
            skLineSegment(sketch, "E118.2.0", {"start": v(-8204.2, 1066.8) * mm, "end": v(-8204.2, 2082.8) * mm});
            skLineSegment(sketch, "E118.2.1", {"start": v(-8204.2, 2082.8) * mm, "end": v(-7543.8, 2082.8) * mm});
            skLineSegment(sketch, "E118.2.2", {"start": v(-7543.8, 2082.8) * mm, "end": v(-7543.8, 1066.8) * mm});
            skLineSegment(sketch, "E118.2.3", {"start": v(-7543.8, 1066.8) * mm, "end": v(-8204.2, 1066.8) * mm});
            skLineSegment(sketch, "E118.3.0", {"start": v(-6781.8, 1066.8) * mm, "end": v(-6781.8, 2082.8) * mm});
            skLineSegment(sketch, "E118.3.1", {"start": v(-6781.8, 2082.8) * mm, "end": v(-6121.4, 2082.8) * mm});
            skLineSegment(sketch, "E118.3.2", {"start": v(-6121.4, 2082.8) * mm, "end": v(-6121.4, 1066.8) * mm});
            skLineSegment(sketch, "E118.3.3", {"start": v(-6121.4, 1066.8) * mm, "end": v(-6781.8, 1066.8) * mm});
            skLineSegment(sketch, "E118.4.0", {"start": v(-3378.2, 1066.8) * mm, "end": v(-3378.2, 2082.8) * mm});
            skLineSegment(sketch, "E118.4.1", {"start": v(-3378.2, 2082.8) * mm, "end": v(-2717.8, 2082.8) * mm});
            skLineSegment(sketch, "E118.4.2", {"start": v(-2717.8, 2082.8) * mm, "end": v(-2717.8, 1066.8) * mm});
            skLineSegment(sketch, "E118.4.3", {"start": v(-2717.8, 1066.8) * mm, "end": v(-3378.2, 1066.8) * mm});
            skLineSegment(sketch, "E118.5.0", {"start": v(-1905, 1066.8) * mm, "end": v(-1905, 2082.8) * mm});
            skLineSegment(sketch, "E118.5.1", {"start": v(-1905, 2082.8) * mm, "end": v(-1244.6, 2082.8) * mm});
            skLineSegment(sketch, "E118.5.2", {"start": v(-1244.6, 2082.8) * mm, "end": v(-1244.6, 1066.8) * mm});
            skLineSegment(sketch, "E118.5.3", {"start": v(-1244.6, 1066.8) * mm, "end": v(-1905, 1066.8) * mm});
            skLineSegment(sketch, "E118.6.0", {"start": v(-2463.8, 3429) * mm, "end": v(-2463.8, 4445) * mm});
            skLineSegment(sketch, "E118.6.1", {"start": v(-2463.8, 4445) * mm, "end": v(-1803.4, 4445) * mm});
            skLineSegment(sketch, "E118.6.2", {"start": v(-1803.4, 4445) * mm, "end": v(-1803.4, 3429) * mm});
            skLineSegment(sketch, "E118.6.3", {"start": v(-1803.4, 3429) * mm, "end": v(-2463.8, 3429) * mm});
            skLineSegment(sketch, "E118.7.0", {"start": v(-4978.4, 3429) * mm, "end": v(-4978.4, 4445) * mm});
            skLineSegment(sketch, "E118.7.1", {"start": v(-4978.4, 4445) * mm, "end": v(-4318, 4445) * mm});
            skLineSegment(sketch, "E118.7.2", {"start": v(-4318, 4445) * mm, "end": v(-4318, 3429) * mm});
            skLineSegment(sketch, "E118.7.3", {"start": v(-4318, 3429) * mm, "end": v(-4978.4, 3429) * mm});
            skLineSegment(sketch, "E118.8.0", {"start": v(-7506.89, 3429) * mm, "end": v(-7506.89, 4445) * mm});
            skLineSegment(sketch, "E118.8.1", {"start": v(-7506.89, 4445) * mm, "end": v(-6846.49, 4445) * mm});
            skLineSegment(sketch, "E118.8.2", {"start": v(-6846.49, 4445) * mm, "end": v(-6846.49, 3429) * mm});
            skLineSegment(sketch, "E118.8.3", {"start": v(-6846.49, 3429) * mm, "end": v(-7506.89, 3429) * mm});
            skLineSegment(sketch, "E118.9.0", {"start": v(-10668, 3429) * mm, "end": v(-10668, 4445) * mm});
            skLineSegment(sketch, "E118.9.1", {"start": v(-10668, 4445) * mm, "end": v(-10007.6, 4445) * mm});
            skLineSegment(sketch, "E118.9.2", {"start": v(-10007.6, 4445) * mm, "end": v(-10007.6, 3429) * mm});
            skLineSegment(sketch, "E118.9.3", {"start": v(-10007.6, 3429) * mm, "end": v(-10668, 3429) * mm});
            skLineSegment(sketch, "E118.10.0", {"start": v(-11963.4, 5252.45) * mm, "end": v(-11963.4, 6116.05) * mm});
            skLineSegment(sketch, "E118.10.1", {"start": v(-11963.4, 6116.05) * mm, "end": v(-11404.6, 6116.05) * mm});
            skLineSegment(sketch, "E118.10.2", {"start": v(-11404.6, 6116.05) * mm, "end": v(-11404.6, 5252.45) * mm});
            skLineSegment(sketch, "E118.10.3", {"start": v(-11404.6, 5252.45) * mm, "end": v(-11963.4, 5252.45) * mm});
            skLineSegment(sketch, "E118.11.0", {"start": v(-13487.4, 3429) * mm, "end": v(-13487.4, 4445) * mm});
            skLineSegment(sketch, "E118.11.1", {"start": v(-13487.4, 4445) * mm, "end": v(-12827, 4445) * mm});
            skLineSegment(sketch, "E118.11.2", {"start": v(-12827, 4445) * mm, "end": v(-12827, 3429) * mm});
            skLineSegment(sketch, "E118.11.3", {"start": v(-12827, 3429) * mm, "end": v(-13487.4, 3429) * mm});
            skSolve(sketch);
        }
        {
            var Q0;
            Q0 = qSketchRegion(id + "F70", true);
            extrude(context, id + "F71", {"entities" : qUnion([Q0]), "operationType" : NewBodyOperationType.REMOVE, "oppositeDirection" : true, "depth" : 76.2 * mm});
        }
        {
            var Q0;
            Q0=makeQuery(id+"F55.opExtrude","CAP_FACE",FACE,{"disambiguationData":[OSD([sQuery(id+"F54.wireOp",EDGE,"E78.bottom"),sQuery(id+"F54.wireOp",EDGE,"E78.top"),sQuery(id+"F54.wireOp",EDGE,"E78.left"),sQuery(id+"F54.wireOp",EDGE,"E78.right")])],"isStart":true});
            var sketch = newSketch(context, id + "F72", { "sketchPlane" : qUnion([Q0])});
            skLineSegment(sketch, "E119.0.0", {"start": v(-9296.4, 330.2) * mm, "end": v(-10058.4, 330.2) * mm});
            skLineSegment(sketch, "E119.0.1", {"start": v(-10058.4, 330.2) * mm, "end": v(-10058.4, 2311.4) * mm});
            skLineSegment(sketch, "E119.0.2", {"start": v(-10058.4, 2311.4) * mm, "end": v(-9296.4, 2311.4) * mm});
            skLineSegment(sketch, "E119.0.3", {"start": v(-9296.4, 2311.4) * mm, "end": v(-9296.4, 330.2) * mm});
            skLineSegment(sketch, "E119.1.0", {"start": v(-4267.2, 330.2) * mm, "end": v(-5029.2, 330.2) * mm});
            skLineSegment(sketch, "E119.1.1", {"start": v(-5029.2, 330.2) * mm, "end": v(-5029.2, 2311.4) * mm});
            skLineSegment(sketch, "E119.1.2", {"start": v(-5029.2, 2311.4) * mm, "end": v(-4267.2, 2311.4) * mm});
            skLineSegment(sketch, "E119.1.3", {"start": v(-4267.2, 2311.4) * mm, "end": v(-4267.2, 330.2) * mm});
            skSolve(sketch);
        }
        {
            var Q0;
            Q0 = qSketchRegion(id + "F72", true);
            extrude(context, id + "F73", {"entities" : qUnion([Q0]), "operationType" : NewBodyOperationType.REMOVE, "oppositeDirection" : true, "depth" : 127 * mm});
        }
        {
            var Q0;
            Q0=makeQuery(id+"F39.opExtrude","CAP_FACE",FACE,{"disambiguationData":[OSD([sQuery(id+"F26.wireOp",EDGE,"E43"),sQuery(id+"F26.wireOp",EDGE,"E44"),sQuery(id+"F38.wireOp",EDGE,"E64")])],"isStart":false});
            var sketch = newSketch(context, id + "F74", { "sketchPlane" : qUnion([Q0])});
            skLineSegment(sketch, "E120", {"start": v(-4533.9, 7044.89) * mm, "end": v(-3911.6, 7044.89) * mm});
            skLineSegment(sketch, "E121", {"start": v(-2451.1, 7044.89) * mm, "end": v(-3048, 7044.89) * mm});
            skLineSegment(sketch, "E122", {"start": v(-3911.6, 7667.19) * mm, "end": v(-3073.4, 7667.19) * mm});
            skSolve(sketch);
        }
        {
            var Q0;
            {var subQ6=sQuery(id+"F74.wireOp",EDGE,"E120");Q0=makeQuery(id+"F74.imprint","IMPRINT",FACE,{"disambiguationData":[TD([[makeQuery(id+"F74.imprint","IMPRINT",EDGE,{"derivedFrom":subQ6}),1.0]])]});}
            extrude(context, id + "F75", {"entities" : qUnion([Q0]), "operationType" : NewBodyOperationType.ADD, "depth" : 6.35 * mm});
        }
        {
            var Q0;
            Q0=makeQuery(id+"F21.boolean.opBoolean","SPLIT",FACE,{"disambiguationData":[TD([makeQuery(id+"F1.opExtrude","CAP_FACE",FACE,{"disambiguationData":[OSD([sQuery(id+"F0.wireOp",EDGE,"E0.bottom"),sQuery(id+"F0.wireOp",EDGE,"E0.top"),sQuery(id+"F0.wireOp",EDGE,"E0.left"),sQuery(id+"F0.wireOp",EDGE,"E0.right")])],"isStart":true})])],"derivedFrom":makeQuery(id+"F14.boolean.opBoolean","COPY",FACE,{"derivedFrom":makeQuery(id+"F14.opExtrude","SWEPT_FACE",FACE,{"disambiguationData":[OSD([sQuery(id+"F13.wireOp",EDGE,"E19.right")])]})})});
            var sketch = newSketch(context, id + "F76", { "sketchPlane" : qUnion([Q0])});
            skLineSegment(sketch, "E123.bottom", {"start": v(701.95, 0) * mm, "end": v(5947.56, 0) * mm});
            skLineSegment(sketch, "E123.top", {"start": v(701.95, 152.4) * mm, "end": v(5947.56, 152.4) * mm});
            skLineSegment(sketch, "E123.left", {"start": v(701.95, 0) * mm, "end": v(701.95, 152.4) * mm});
            skLineSegment(sketch, "E123.right", {"start": v(5947.56, 0) * mm, "end": v(5947.56, 152.4) * mm});
            skSolve(sketch);
        }
        {
            var Q0;
            Q0 = qSketchRegion(id + "F76", true);
            extrude(context, id + "F77", {"entities" : qUnion([Q0]), "operationType" : NewBodyOperationType.ADD, "depth" : 3657.6 * mm});
        }
        {
            var Q0;
            Q0=makeQuery(id+"F77.opExtrude","SWEPT_FACE",FACE,{"disambiguationData":[OSD([sQuery(id+"F76.wireOp",EDGE,"E123.top")])]});
            var sketch = newSketch(context, id + "F78", { "sketchPlane" : qUnion([Q0])});
            skLineSegment(sketch, "E124.bottom", {"start": v(-828.95, 16894.23) * mm, "end": v(-740.05, 16894.23) * mm});
            skLineSegment(sketch, "E124.top", {"start": v(-828.95, 16805.33) * mm, "end": v(-740.05, 16805.33) * mm});
            skLineSegment(sketch, "E124.left", {"start": v(-828.95, 16894.23) * mm, "end": v(-828.95, 16805.33) * mm});
            skLineSegment(sketch, "E124.right", {"start": v(-740.05, 16894.23) * mm, "end": v(-740.05, 16805.33) * mm});
            skLineSegment(sketch, "E125.bottom", {"start": v(-828.95, 18453.1) * mm, "end": v(-740.05, 18453.1) * mm});
            skLineSegment(sketch, "E125.top", {"start": v(-828.95, 18364.2) * mm, "end": v(-740.05, 18364.2) * mm});
            skLineSegment(sketch, "E125.left", {"start": v(-828.95, 18453.1) * mm, "end": v(-828.95, 18364.2) * mm});
            skLineSegment(sketch, "E125.right", {"start": v(-740.05, 18453.1) * mm, "end": v(-740.05, 18364.2) * mm});
            skLineSegment(sketch, "E126.bottom", {"start": v(-2035.45, 18453.1) * mm, "end": v(-1946.55, 18453.1) * mm});
            skLineSegment(sketch, "E126.top", {"start": v(-2035.45, 18364.2) * mm, "end": v(-1946.55, 18364.2) * mm});
            skLineSegment(sketch, "E126.left", {"start": v(-2035.45, 18453.1) * mm, "end": v(-2035.45, 18364.2) * mm});
            skLineSegment(sketch, "E126.right", {"start": v(-1946.55, 18453.1) * mm, "end": v(-1946.55, 18364.2) * mm});
            skLineSegment(sketch, "E127.bottom", {"start": v(-3241.95, 18453.1) * mm, "end": v(-3153.05, 18453.1) * mm});
            skLineSegment(sketch, "E127.top", {"start": v(-3241.95, 18364.2) * mm, "end": v(-3153.05, 18364.2) * mm});
            skLineSegment(sketch, "E127.left", {"start": v(-3241.95, 18453.1) * mm, "end": v(-3241.95, 18364.2) * mm});
            skLineSegment(sketch, "E127.right", {"start": v(-3153.05, 18453.1) * mm, "end": v(-3153.05, 18364.2) * mm});
            skLineSegment(sketch, "E128.bottom", {"start": v(-4448.45, 18453.1) * mm, "end": v(-4359.55, 18453.1) * mm});
            skLineSegment(sketch, "E128.top", {"start": v(-4448.45, 18364.2) * mm, "end": v(-4359.55, 18364.2) * mm});
            skLineSegment(sketch, "E128.left", {"start": v(-4448.45, 18453.1) * mm, "end": v(-4448.45, 18364.2) * mm});
            skLineSegment(sketch, "E128.right", {"start": v(-4359.55, 18453.1) * mm, "end": v(-4359.55, 18364.2) * mm});
            skLineSegment(sketch, "E129", {"start": v(-4359.55, 18364.2) * mm, "end": v(-3241.95, 18364.2) * mm});
            skLineSegment(sketch, "E130", {"start": v(-2035.45, 18364.2) * mm, "end": v(-3153.05, 18364.2) * mm});
            skLineSegment(sketch, "E131", {"start": v(-1946.55, 18364.2) * mm, "end": v(-828.95, 18364.2) * mm});
            skSolve(sketch);
        }
        {
            var Q0;
            Q0=makeQuery(id+"F78.imprint","IMPRINT",FACE,{"disambiguationData":[TD([[makeQuery(id+"F78.imprint","IMPRINT",EDGE,{"derivedFrom":sQuery(id+"F78.wireOp",EDGE,"E128.bottom")}),-1.0]])]});
            var Q1;
            Q1=makeQuery(id+"F78.imprint","IMPRINT",FACE,{"disambiguationData":[TD([[makeQuery(id+"F78.imprint","IMPRINT",EDGE,{"derivedFrom":sQuery(id+"F78.wireOp",EDGE,"E127.bottom")}),-1.0]])]});
            var Q2;
            Q2=makeQuery(id+"F78.imprint","IMPRINT",FACE,{"disambiguationData":[TD([[makeQuery(id+"F78.imprint","IMPRINT",EDGE,{"derivedFrom":sQuery(id+"F78.wireOp",EDGE,"E126.bottom")}),-1.0]])]});
            var Q3;
            Q3=makeQuery(id+"F78.imprint","IMPRINT",FACE,{"disambiguationData":[TD([[makeQuery(id+"F78.imprint","IMPRINT",EDGE,{"derivedFrom":sQuery(id+"F78.wireOp",EDGE,"E125.bottom")}),-1.0]])]});
            var Q4;
            Q4=makeQuery(id+"F78.imprint","IMPRINT",FACE,{"disambiguationData":[TD([[makeQuery(id+"F78.imprint","IMPRINT",EDGE,{"derivedFrom":sQuery(id+"F78.wireOp",EDGE,"E124.bottom")}),-1.0]])]});
            extrude(context, id + "F79", {"entities" : qUnion([Q0, Q1, Q2, Q3, Q4]), "operationType" : NewBodyOperationType.ADD, "depth" : 1828.8 * mm, "hasSecondDirection" : true, "secondDirectionOppositeDirection" : true, "secondDirectionDepth" : 609.6 * mm});
        }
        {
            var Q0;
            {var subQ1=sQuery(id+"F78.wireOp",EDGE,"E124.right");Q0=makeQuery(id+"F79.boolean.opBoolean","SPLIT",FACE,{"disambiguationData":[TD([makeQuery(id+"F77.opExtrude","SWEPT_FACE",FACE,{"disambiguationData":[OSD([sQuery(id+"F76.wireOp",EDGE,"E123.top")])]})])],"derivedFrom":makeQuery(id+"F79.opExtrude","SWEPT_FACE",FACE,{"disambiguationData":[OSD([subQ1])]})});}
            var sketch = newSketch(context, id + "F80", { "sketchPlane" : qUnion([Q0])});
            skLineSegment(sketch, "E132.bottom", {"start": v(16805.33, 1879.6) * mm, "end": v(18427.7, 1879.6) * mm});
            skLineSegment(sketch, "E132.top", {"start": v(16805.33, 660.4) * mm, "end": v(18427.7, 660.4) * mm});
            skLineSegment(sketch, "E132.left", {"start": v(16805.33, 1879.6) * mm, "end": v(16805.33, 660.4) * mm});
            skLineSegment(sketch, "E132.right", {"start": v(18427.7, 1879.6) * mm, "end": v(18427.7, 660.4) * mm});
            skSolve(sketch);
        }
        {
            var Q0;
            Q0 = qSketchRegion(id + "F80", true);
            extrude(context, id + "F81", {"entities" : qUnion([Q0]), "operationType" : NewBodyOperationType.ADD, "depth" : 12.7 * mm});
        }
        {
            var Q0;
            {var subQ2=sQuery(id+"F78.wireOp",EDGE,"E126.bottom");Q0=makeQuery(id+"F79.boolean.opBoolean","SPLIT",FACE,{"disambiguationData":[TD([makeQuery(id+"F77.opExtrude","SWEPT_FACE",FACE,{"disambiguationData":[OSD([sQuery(id+"F76.wireOp",EDGE,"E123.top")])]})])],"derivedFrom":makeQuery(id+"F79.opExtrude","SWEPT_FACE",FACE,{"disambiguationData":[OSD([subQ2])]})});}
            var sketch = newSketch(context, id + "F82", { "sketchPlane" : qUnion([Q0])});
            skLineSegment(sketch, "E133.bottom", {"start": v(765.45, 1879.6) * mm, "end": v(4423.05, 1879.6) * mm});
            skLineSegment(sketch, "E133.top", {"start": v(765.45, 660.4) * mm, "end": v(4423.05, 660.4) * mm});
            skLineSegment(sketch, "E133.left", {"start": v(765.45, 1879.6) * mm, "end": v(765.45, 660.4) * mm});
            skLineSegment(sketch, "E133.right", {"start": v(4423.05, 1879.6) * mm, "end": v(4423.05, 660.4) * mm});
            skSolve(sketch);
        }
        {
            var Q0;
            Q0 = qSketchRegion(id + "F82", true);
            extrude(context, id + "F83", {"entities" : qUnion([Q0]), "operationType" : NewBodyOperationType.ADD, "depth" : 12.7 * mm});
        }
        {
            var Q0;
            Q0=makeQuery(id+"F53.opExtrude","CAP_FACE",FACE,{"disambiguationData":[OSD([sQuery(id+"F52.wireOp",EDGE,"E71.0"),sQuery(id+"F52.wireOp",EDGE,"E71.1"),sQuery(id+"F52.wireOp",EDGE,"E71.2"),sQuery(id+"F52.wireOp",EDGE,"E71.3")])],"isStart":false});
            var sketch = newSketch(context, id + "F84", { "sketchPlane" : qUnion([Q0])});
            skLineSegment(sketch, "E134.0", {"start": v(-6400.8, -584.2) * mm, "end": v(-6400.8, -14554.2) * mm});
            skLineSegment(sketch, "E134.1", {"start": v(-584.2, -584.2) * mm, "end": v(-6400.8, -584.2) * mm});
            skLineSegment(sketch, "E134.2", {"start": v(-584.2, -14554.2) * mm, "end": v(-584.2, -584.2) * mm});
            skLineSegment(sketch, "E134.3", {"start": v(-6400.8, -14554.2) * mm, "end": v(-584.2, -14554.2) * mm});
            skSolve(sketch);
        }
        {
            var Q0;
            Q0 = qSketchRegion(id + "F84", true);
            extrude(context, id + "F85", {"entities" : qUnion([Q0]), "operationType" : NewBodyOperationType.REMOVE, "oppositeDirection" : true, "depth" : 5232.4 * mm});
        }
        {
            var Q0;
            Q0=makeQuery(id+"F85.boolean.opBoolean","COPY",FACE,{"derivedFrom":makeQuery(id+"F85.opExtrude","CAP_FACE",FACE,{"disambiguationData":[OSD([sQuery(id+"F84.wireOp",EDGE,"E134.0"),sQuery(id+"F84.wireOp",EDGE,"E134.1"),sQuery(id+"F84.wireOp",EDGE,"E134.2"),sQuery(id+"F84.wireOp",EDGE,"E134.3")])],"isStart":false})});
            var sketch = newSketch(context, id + "F86", { "sketchPlane" : qUnion([Q0])});
            skLineSegment(sketch, "E135.bottom", {"start": v(-6400.8, -12866.06) * mm, "end": v(-6324.6, -12866.06) * mm});
            skLineSegment(sketch, "E135.top", {"start": v(-6400.8, -12789.86) * mm, "end": v(-6324.6, -12789.86) * mm});
            skLineSegment(sketch, "E135.left", {"start": v(-6400.8, -12866.06) * mm, "end": v(-6400.8, -12789.86) * mm});
            skLineSegment(sketch, "E135.right", {"start": v(-6324.6, -12866.06) * mm, "end": v(-6324.6, -12789.86) * mm});
            skSolve(sketch);
        }
        {
            var Q0;
            Q0 = qSketchRegion(id + "F86", true);
            extrude(context, id + "F87", {"entities" : qUnion([Q0]), "operationType" : NewBodyOperationType.ADD, "oppositeDirection" : true, "depth" : 3276.6 * mm});
        }
        {
            var Q0;
            Q0=makeQuery(id+"F85.boolean.opBoolean","COPY",FACE,{"derivedFrom":makeQuery(id+"F85.opExtrude","CAP_FACE",FACE,{"disambiguationData":[OSD([sQuery(id+"F84.wireOp",EDGE,"E134.0"),sQuery(id+"F84.wireOp",EDGE,"E134.1"),sQuery(id+"F84.wireOp",EDGE,"E134.2"),sQuery(id+"F84.wireOp",EDGE,"E134.3")])],"isStart":false})});
            var sketch = newSketch(context, id + "F88", { "sketchPlane" : qUnion([Q0])});
            skLineSegment(sketch, "E136.bottom", {"start": v(-665.4, -6410.83) * mm, "end": v(-589.2, -6410.83) * mm});
            skLineSegment(sketch, "E136.top", {"start": v(-665.4, -6334.63) * mm, "end": v(-589.2, -6334.63) * mm});
            skLineSegment(sketch, "E136.left", {"start": v(-665.4, -6410.83) * mm, "end": v(-665.4, -6334.63) * mm});
            skLineSegment(sketch, "E136.right", {"start": v(-589.2, -6410.83) * mm, "end": v(-589.2, -6334.63) * mm});
            skSolve(sketch);
        }
        {
            var Q0;
            Q0 = qSketchRegion(id + "F88", true);
            extrude(context, id + "F89", {"entities" : qUnion([Q0]), "operationType" : NewBodyOperationType.ADD, "oppositeDirection" : true, "depth" : 2946.4 * mm});
        }
    });
